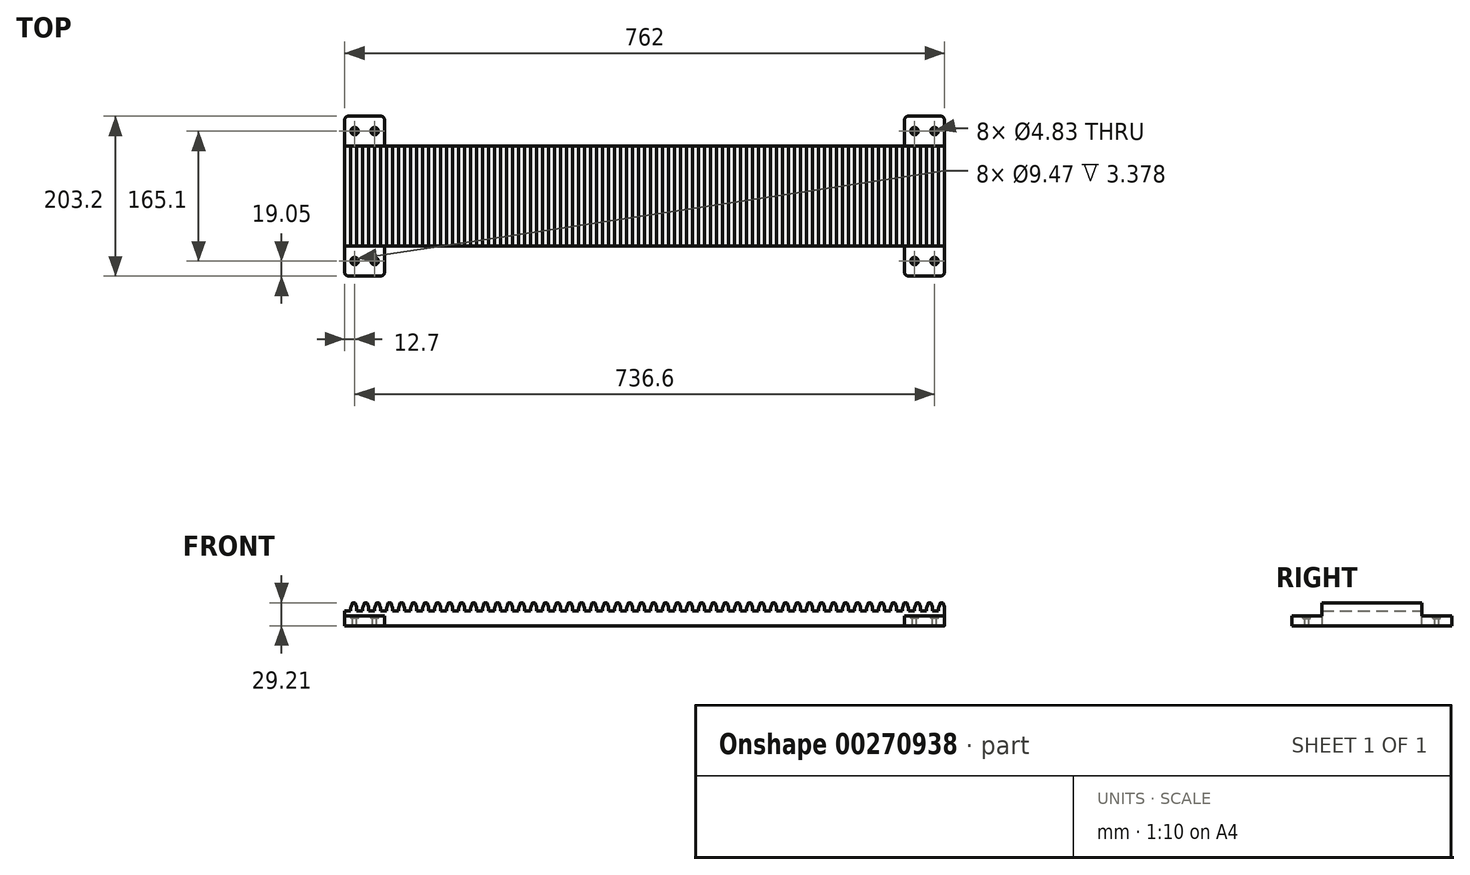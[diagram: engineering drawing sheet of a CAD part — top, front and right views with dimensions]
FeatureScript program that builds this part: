
annotation { "Feature Type Name" : "Feature", "Feature Type Description" : "" }
export const myFeature = defineFeature(function(context is Context, id is Id, definition is map)
    precondition{}
    {
        {
            var Q0;
            Q0=qCreatedBy(makeId("Front.planeOp"),FACE);
            var sketch = newSketch(context, id + "F0", { "sketchPlane" : qUnion([Q0])});
            skLineSegment(sketch, "E0", {"start": v(0, 0) * mm, "end": v(7.62, 0) * mm});
            skLineSegment(sketch, "E1", {"start": v(7.62, 0) * mm, "end": v(7.62, 2.76) * mm});
            skLineSegment(sketch, "E2", {"start": v(7.62, 0) * mm, "end": v(15.24, 0) * mm});
            skLineSegment(sketch, "E3", {"start": v(15.24, 0) * mm, "end": v(15.24, 2.76) * mm});
            skLineSegment(sketch, "E4", {"start": v(9.77, 9.65) * mm, "end": v(8.02, 4.99) * mm});
            skLineSegment(sketch, "E5", {"start": v(13.1, 9.65) * mm, "end": v(14.84, 4.99) * mm});
            skLineSegment(sketch, "E6", {"start": v(10.5, 10.16) * mm, "end": v(12.36, 10.16) * mm});
            skPoint(sketch, "E7.visualSharp", {"position": v(9.96, 10.16) * mm});
            skArc(sketch, "E7.filletArc", {"start": v(10.5, 10.16) * mm, "mid": v(10.05, 10.02) * mm, "end": v(9.77, 9.65) * mm});
            skPoint(sketch, "E8.visualSharp", {"position": v(12.9, 10.16) * mm});
            skArc(sketch, "E8.filletArc", {"start": v(13.1, 9.65) * mm, "mid": v(12.8, 10.02) * mm, "end": v(12.36, 10.16) * mm});
            skPoint(sketch, "E9.visualSharp", {"position": v(7.62, 3.91) * mm});
            skArc(sketch, "E9.filletArc", {"start": v(8.02, 4.99) * mm, "mid": v(7.72, 3.9) * mm, "end": v(7.62, 2.76) * mm});
            skPoint(sketch, "E10.visualSharp", {"position": v(15.24, 3.91) * mm});
            skArc(sketch, "E10.filletArc", {"start": v(15.24, 2.76) * mm, "mid": v(15.14, 3.9) * mm, "end": v(14.84, 4.99) * mm});
            skLineSegment(sketch, "E11", {"start": v(0, 0) * mm, "end": v(0, -19.05) * mm});
            skLineSegment(sketch, "E12", {"start": v(0, -19.05) * mm, "end": v(762, -19.05) * mm});
            skLineSegment(sketch, "E13", {"start": v(762, 0) * mm, "end": v(15.24, 0) * mm});
            skLineSegment(sketch, "E14", {"start": v(15.24, 0) * mm, "end": v(22.86, 0) * mm});
            skLineSegment(sketch, "E15.1.0.0", {"start": v(22.86, 0) * mm, "end": v(22.86, 2.76) * mm});
            skArc(sketch, "E15.1.0.1", {"start": v(23.26, 4.99) * mm, "mid": v(22.96, 3.9) * mm, "end": v(22.86, 2.76) * mm});
            skLineSegment(sketch, "E15.1.0.2", {"start": v(25, 9.65) * mm, "end": v(23.26, 4.99) * mm});
            skArc(sketch, "E15.1.0.3", {"start": v(25.74, 10.16) * mm, "mid": v(25.3, 10.02) * mm, "end": v(25, 9.65) * mm});
            skLineSegment(sketch, "E15.1.0.4", {"start": v(25.74, 10.16) * mm, "end": v(27.6, 10.16) * mm});
            skArc(sketch, "E15.1.0.5", {"start": v(28.33, 9.65) * mm, "mid": v(28.05, 10.02) * mm, "end": v(27.6, 10.16) * mm});
            skLineSegment(sketch, "E15.1.0.6", {"start": v(28.33, 9.65) * mm, "end": v(30.08, 4.99) * mm});
            skArc(sketch, "E15.1.0.7", {"start": v(30.48, 2.76) * mm, "mid": v(30.38, 3.9) * mm, "end": v(30.08, 4.99) * mm});
            skLineSegment(sketch, "E15.1.0.8", {"start": v(30.48, 0) * mm, "end": v(30.48, 2.76) * mm});
            skLineSegment(sketch, "E15.2.0.0", {"start": v(38.1, 0) * mm, "end": v(38.1, 2.76) * mm});
            skArc(sketch, "E15.2.0.1", {"start": v(38.5, 4.99) * mm, "mid": v(38.2, 3.9) * mm, "end": v(38.1, 2.76) * mm});
            skLineSegment(sketch, "E15.2.0.2", {"start": v(40.25, 9.65) * mm, "end": v(38.5, 4.99) * mm});
            skArc(sketch, "E15.2.0.3", {"start": v(40.98, 10.16) * mm, "mid": v(40.53, 10.02) * mm, "end": v(40.25, 9.65) * mm});
            skLineSegment(sketch, "E15.2.0.4", {"start": v(40.98, 10.16) * mm, "end": v(42.84, 10.16) * mm});
            skArc(sketch, "E15.2.0.5", {"start": v(43.57, 9.65) * mm, "mid": v(43.29, 10.02) * mm, "end": v(42.84, 10.16) * mm});
            skLineSegment(sketch, "E15.2.0.6", {"start": v(43.57, 9.65) * mm, "end": v(45.32, 4.99) * mm});
            skArc(sketch, "E15.2.0.7", {"start": v(45.72, 2.76) * mm, "mid": v(45.62, 3.9) * mm, "end": v(45.32, 4.99) * mm});
            skLineSegment(sketch, "E15.2.0.8", {"start": v(45.72, 0) * mm, "end": v(45.72, 2.76) * mm});
            skLineSegment(sketch, "E15.3.0.0", {"start": v(53.34, 0) * mm, "end": v(53.34, 2.76) * mm});
            skArc(sketch, "E15.3.0.1", {"start": v(53.74, 4.99) * mm, "mid": v(53.44, 3.9) * mm, "end": v(53.34, 2.76) * mm});
            skLineSegment(sketch, "E15.3.0.2", {"start": v(55.49, 9.65) * mm, "end": v(53.74, 4.99) * mm});
            skArc(sketch, "E15.3.0.3", {"start": v(56.22, 10.16) * mm, "mid": v(55.77, 10.02) * mm, "end": v(55.49, 9.65) * mm});
            skLineSegment(sketch, "E15.3.0.4", {"start": v(56.22, 10.16) * mm, "end": v(58.08, 10.16) * mm});
            skArc(sketch, "E15.3.0.5", {"start": v(58.81, 9.65) * mm, "mid": v(58.53, 10.02) * mm, "end": v(58.08, 10.16) * mm});
            skLineSegment(sketch, "E15.3.0.6", {"start": v(58.81, 9.65) * mm, "end": v(60.56, 4.99) * mm});
            skArc(sketch, "E15.3.0.7", {"start": v(60.96, 2.76) * mm, "mid": v(60.86, 3.9) * mm, "end": v(60.56, 4.99) * mm});
            skLineSegment(sketch, "E15.3.0.8", {"start": v(60.96, 0) * mm, "end": v(60.96, 2.76) * mm});
            skLineSegment(sketch, "E15.4.0.0", {"start": v(68.58, 0) * mm, "end": v(68.58, 2.76) * mm});
            skArc(sketch, "E15.4.0.1", {"start": v(68.98, 4.99) * mm, "mid": v(68.68, 3.9) * mm, "end": v(68.58, 2.76) * mm});
            skLineSegment(sketch, "E15.4.0.2", {"start": v(70.73, 9.65) * mm, "end": v(68.98, 4.99) * mm});
            skArc(sketch, "E15.4.0.3", {"start": v(71.46, 10.16) * mm, "mid": v(71.01, 10.02) * mm, "end": v(70.73, 9.65) * mm});
            skLineSegment(sketch, "E15.4.0.4", {"start": v(71.46, 10.16) * mm, "end": v(73.32, 10.16) * mm});
            skArc(sketch, "E15.4.0.5", {"start": v(74.05, 9.65) * mm, "mid": v(73.77, 10.02) * mm, "end": v(73.32, 10.16) * mm});
            skLineSegment(sketch, "E15.4.0.6", {"start": v(74.05, 9.65) * mm, "end": v(75.8, 4.99) * mm});
            skArc(sketch, "E15.4.0.7", {"start": v(76.2, 2.76) * mm, "mid": v(76.1, 3.9) * mm, "end": v(75.8, 4.99) * mm});
            skLineSegment(sketch, "E15.4.0.8", {"start": v(76.2, 0) * mm, "end": v(76.2, 2.76) * mm});
            skLineSegment(sketch, "E15.5.0.0", {"start": v(83.82, 0) * mm, "end": v(83.82, 2.76) * mm});
            skArc(sketch, "E15.5.0.1", {"start": v(84.22, 4.99) * mm, "mid": v(83.92, 3.9) * mm, "end": v(83.82, 2.76) * mm});
            skLineSegment(sketch, "E15.5.0.2", {"start": v(85.97, 9.65) * mm, "end": v(84.22, 4.99) * mm});
            skArc(sketch, "E15.5.0.3", {"start": v(86.7, 10.16) * mm, "mid": v(86.25, 10.02) * mm, "end": v(85.97, 9.65) * mm});
            skLineSegment(sketch, "E15.5.0.4", {"start": v(86.7, 10.16) * mm, "end": v(88.56, 10.16) * mm});
            skArc(sketch, "E15.5.0.5", {"start": v(89.3, 9.65) * mm, "mid": v(89, 10.02) * mm, "end": v(88.56, 10.16) * mm});
            skLineSegment(sketch, "E15.5.0.6", {"start": v(89.3, 9.65) * mm, "end": v(91.04, 4.99) * mm});
            skArc(sketch, "E15.5.0.7", {"start": v(91.44, 2.76) * mm, "mid": v(91.34, 3.9) * mm, "end": v(91.04, 4.99) * mm});
            skLineSegment(sketch, "E15.5.0.8", {"start": v(91.44, 0) * mm, "end": v(91.44, 2.76) * mm});
            skLineSegment(sketch, "E15.6.0.0", {"start": v(99.06, 0) * mm, "end": v(99.06, 2.76) * mm});
            skArc(sketch, "E15.6.0.1", {"start": v(99.46, 4.99) * mm, "mid": v(99.16, 3.9) * mm, "end": v(99.06, 2.76) * mm});
            skLineSegment(sketch, "E15.6.0.2", {"start": v(101.2, 9.65) * mm, "end": v(99.46, 4.99) * mm});
            skArc(sketch, "E15.6.0.3", {"start": v(101.94, 10.16) * mm, "mid": v(101.5, 10.02) * mm, "end": v(101.2, 9.65) * mm});
            skLineSegment(sketch, "E15.6.0.4", {"start": v(101.94, 10.16) * mm, "end": v(103.8, 10.16) * mm});
            skArc(sketch, "E15.6.0.5", {"start": v(104.53, 9.65) * mm, "mid": v(104.25, 10.02) * mm, "end": v(103.8, 10.16) * mm});
            skLineSegment(sketch, "E15.6.0.6", {"start": v(104.53, 9.65) * mm, "end": v(106.28, 4.99) * mm});
            skArc(sketch, "E15.6.0.7", {"start": v(106.68, 2.76) * mm, "mid": v(106.58, 3.9) * mm, "end": v(106.28, 4.99) * mm});
            skLineSegment(sketch, "E15.6.0.8", {"start": v(106.68, 0) * mm, "end": v(106.68, 2.76) * mm});
            skLineSegment(sketch, "E15.7.0.0", {"start": v(114.3, 0) * mm, "end": v(114.3, 2.76) * mm});
            skArc(sketch, "E15.7.0.1", {"start": v(114.7, 4.99) * mm, "mid": v(114.4, 3.9) * mm, "end": v(114.3, 2.76) * mm});
            skLineSegment(sketch, "E15.7.0.2", {"start": v(116.45, 9.65) * mm, "end": v(114.7, 4.99) * mm});
            skArc(sketch, "E15.7.0.3", {"start": v(117.18, 10.16) * mm, "mid": v(116.73, 10.02) * mm, "end": v(116.45, 9.65) * mm});
            skLineSegment(sketch, "E15.7.0.4", {"start": v(117.18, 10.16) * mm, "end": v(119.04, 10.16) * mm});
            skArc(sketch, "E15.7.0.5", {"start": v(119.77, 9.65) * mm, "mid": v(119.49, 10.02) * mm, "end": v(119.04, 10.16) * mm});
            skLineSegment(sketch, "E15.7.0.6", {"start": v(119.77, 9.65) * mm, "end": v(121.52, 4.99) * mm});
            skArc(sketch, "E15.7.0.7", {"start": v(121.92, 2.76) * mm, "mid": v(121.82, 3.9) * mm, "end": v(121.52, 4.99) * mm});
            skLineSegment(sketch, "E15.7.0.8", {"start": v(121.92, 0) * mm, "end": v(121.92, 2.76) * mm});
            skLineSegment(sketch, "E15.8.0.0", {"start": v(129.54, 0) * mm, "end": v(129.54, 2.76) * mm});
            skArc(sketch, "E15.8.0.1", {"start": v(129.94, 4.99) * mm, "mid": v(129.64, 3.9) * mm, "end": v(129.54, 2.76) * mm});
            skLineSegment(sketch, "E15.8.0.2", {"start": v(131.69, 9.65) * mm, "end": v(129.94, 4.99) * mm});
            skArc(sketch, "E15.8.0.3", {"start": v(132.42, 10.16) * mm, "mid": v(131.97, 10.02) * mm, "end": v(131.69, 9.65) * mm});
            skLineSegment(sketch, "E15.8.0.4", {"start": v(132.42, 10.16) * mm, "end": v(134.28, 10.16) * mm});
            skArc(sketch, "E15.8.0.5", {"start": v(135.01, 9.65) * mm, "mid": v(134.73, 10.02) * mm, "end": v(134.28, 10.16) * mm});
            skLineSegment(sketch, "E15.8.0.6", {"start": v(135.01, 9.65) * mm, "end": v(136.76, 4.99) * mm});
            skArc(sketch, "E15.8.0.7", {"start": v(137.16, 2.76) * mm, "mid": v(137.06, 3.9) * mm, "end": v(136.76, 4.99) * mm});
            skLineSegment(sketch, "E15.8.0.8", {"start": v(137.16, 0) * mm, "end": v(137.16, 2.76) * mm});
            skLineSegment(sketch, "E15.9.0.0", {"start": v(144.78, 0) * mm, "end": v(144.78, 2.76) * mm});
            skArc(sketch, "E15.9.0.1", {"start": v(145.18, 4.99) * mm, "mid": v(144.88, 3.9) * mm, "end": v(144.78, 2.76) * mm});
            skLineSegment(sketch, "E15.9.0.2", {"start": v(146.93, 9.65) * mm, "end": v(145.18, 4.99) * mm});
            skArc(sketch, "E15.9.0.3", {"start": v(147.66, 10.16) * mm, "mid": v(147.21, 10.02) * mm, "end": v(146.93, 9.65) * mm});
            skLineSegment(sketch, "E15.9.0.4", {"start": v(147.66, 10.16) * mm, "end": v(149.52, 10.16) * mm});
            skArc(sketch, "E15.9.0.5", {"start": v(150.25, 9.65) * mm, "mid": v(149.97, 10.02) * mm, "end": v(149.52, 10.16) * mm});
            skLineSegment(sketch, "E15.9.0.6", {"start": v(150.25, 9.65) * mm, "end": v(152, 4.99) * mm});
            skArc(sketch, "E15.9.0.7", {"start": v(152.4, 2.76) * mm, "mid": v(152.3, 3.9) * mm, "end": v(152, 4.99) * mm});
            skLineSegment(sketch, "E15.9.0.8", {"start": v(152.4, 0) * mm, "end": v(152.4, 2.76) * mm});
            skLineSegment(sketch, "E15.10.0.0", {"start": v(160.02, 0) * mm, "end": v(160.02, 2.76) * mm});
            skArc(sketch, "E15.10.0.1", {"start": v(160.42, 4.99) * mm, "mid": v(160.12, 3.9) * mm, "end": v(160.02, 2.76) * mm});
            skLineSegment(sketch, "E15.10.0.2", {"start": v(162.17, 9.65) * mm, "end": v(160.42, 4.99) * mm});
            skArc(sketch, "E15.10.0.3", {"start": v(162.9, 10.16) * mm, "mid": v(162.45, 10.02) * mm, "end": v(162.17, 9.65) * mm});
            skLineSegment(sketch, "E15.10.0.4", {"start": v(162.9, 10.16) * mm, "end": v(164.76, 10.16) * mm});
            skArc(sketch, "E15.10.0.5", {"start": v(165.5, 9.65) * mm, "mid": v(165.2, 10.02) * mm, "end": v(164.76, 10.16) * mm});
            skLineSegment(sketch, "E15.10.0.6", {"start": v(165.5, 9.65) * mm, "end": v(167.24, 4.99) * mm});
            skArc(sketch, "E15.10.0.7", {"start": v(167.64, 2.76) * mm, "mid": v(167.54, 3.9) * mm, "end": v(167.24, 4.99) * mm});
            skLineSegment(sketch, "E15.10.0.8", {"start": v(167.64, 0) * mm, "end": v(167.64, 2.76) * mm});
            skLineSegment(sketch, "E15.11.0.0", {"start": v(175.26, 0) * mm, "end": v(175.26, 2.76) * mm});
            skArc(sketch, "E15.11.0.1", {"start": v(175.66, 4.99) * mm, "mid": v(175.36, 3.9) * mm, "end": v(175.26, 2.76) * mm});
            skLineSegment(sketch, "E15.11.0.2", {"start": v(177.4, 9.65) * mm, "end": v(175.66, 4.99) * mm});
            skArc(sketch, "E15.11.0.3", {"start": v(178.14, 10.16) * mm, "mid": v(177.7, 10.02) * mm, "end": v(177.4, 9.65) * mm});
            skLineSegment(sketch, "E15.11.0.4", {"start": v(178.14, 10.16) * mm, "end": v(180, 10.16) * mm});
            skArc(sketch, "E15.11.0.5", {"start": v(180.73, 9.65) * mm, "mid": v(180.45, 10.02) * mm, "end": v(180, 10.16) * mm});
            skLineSegment(sketch, "E15.11.0.6", {"start": v(180.73, 9.65) * mm, "end": v(182.48, 4.99) * mm});
            skArc(sketch, "E15.11.0.7", {"start": v(182.88, 2.76) * mm, "mid": v(182.78, 3.9) * mm, "end": v(182.48, 4.99) * mm});
            skLineSegment(sketch, "E15.11.0.8", {"start": v(182.88, 0) * mm, "end": v(182.88, 2.76) * mm});
            skLineSegment(sketch, "E15.12.0.0", {"start": v(190.5, 0) * mm, "end": v(190.5, 2.76) * mm});
            skArc(sketch, "E15.12.0.1", {"start": v(190.9, 4.99) * mm, "mid": v(190.6, 3.9) * mm, "end": v(190.5, 2.76) * mm});
            skLineSegment(sketch, "E15.12.0.2", {"start": v(192.65, 9.65) * mm, "end": v(190.9, 4.99) * mm});
            skArc(sketch, "E15.12.0.3", {"start": v(193.38, 10.16) * mm, "mid": v(192.93, 10.02) * mm, "end": v(192.65, 9.65) * mm});
            skLineSegment(sketch, "E15.12.0.4", {"start": v(193.38, 10.16) * mm, "end": v(195.24, 10.16) * mm});
            skArc(sketch, "E15.12.0.5", {"start": v(195.97, 9.65) * mm, "mid": v(195.69, 10.02) * mm, "end": v(195.24, 10.16) * mm});
            skLineSegment(sketch, "E15.12.0.6", {"start": v(195.97, 9.65) * mm, "end": v(197.72, 4.99) * mm});
            skArc(sketch, "E15.12.0.7", {"start": v(198.12, 2.76) * mm, "mid": v(198.02, 3.9) * mm, "end": v(197.72, 4.99) * mm});
            skLineSegment(sketch, "E15.12.0.8", {"start": v(198.12, 0) * mm, "end": v(198.12, 2.76) * mm});
            skLineSegment(sketch, "E15.13.0.0", {"start": v(205.74, 0) * mm, "end": v(205.74, 2.76) * mm});
            skArc(sketch, "E15.13.0.1", {"start": v(206.14, 4.99) * mm, "mid": v(205.84, 3.9) * mm, "end": v(205.74, 2.76) * mm});
            skLineSegment(sketch, "E15.13.0.2", {"start": v(207.89, 9.65) * mm, "end": v(206.14, 4.99) * mm});
            skArc(sketch, "E15.13.0.3", {"start": v(208.62, 10.16) * mm, "mid": v(208.17, 10.02) * mm, "end": v(207.89, 9.65) * mm});
            skLineSegment(sketch, "E15.13.0.4", {"start": v(208.62, 10.16) * mm, "end": v(210.48, 10.16) * mm});
            skArc(sketch, "E15.13.0.5", {"start": v(211.21, 9.65) * mm, "mid": v(210.93, 10.02) * mm, "end": v(210.48, 10.16) * mm});
            skLineSegment(sketch, "E15.13.0.6", {"start": v(211.21, 9.65) * mm, "end": v(212.96, 4.99) * mm});
            skArc(sketch, "E15.13.0.7", {"start": v(213.36, 2.76) * mm, "mid": v(213.26, 3.9) * mm, "end": v(212.96, 4.99) * mm});
            skLineSegment(sketch, "E15.13.0.8", {"start": v(213.36, 0) * mm, "end": v(213.36, 2.76) * mm});
            skLineSegment(sketch, "E15.14.0.0", {"start": v(220.98, 0) * mm, "end": v(220.98, 2.76) * mm});
            skArc(sketch, "E15.14.0.1", {"start": v(221.38, 4.99) * mm, "mid": v(221.08, 3.9) * mm, "end": v(220.98, 2.76) * mm});
            skLineSegment(sketch, "E15.14.0.2", {"start": v(223.13, 9.65) * mm, "end": v(221.38, 4.99) * mm});
            skArc(sketch, "E15.14.0.3", {"start": v(223.86, 10.16) * mm, "mid": v(223.41, 10.02) * mm, "end": v(223.13, 9.65) * mm});
            skLineSegment(sketch, "E15.14.0.4", {"start": v(223.86, 10.16) * mm, "end": v(225.72, 10.16) * mm});
            skArc(sketch, "E15.14.0.5", {"start": v(226.45, 9.65) * mm, "mid": v(226.17, 10.02) * mm, "end": v(225.72, 10.16) * mm});
            skLineSegment(sketch, "E15.14.0.6", {"start": v(226.45, 9.65) * mm, "end": v(228.2, 4.99) * mm});
            skArc(sketch, "E15.14.0.7", {"start": v(228.6, 2.76) * mm, "mid": v(228.5, 3.9) * mm, "end": v(228.2, 4.99) * mm});
            skLineSegment(sketch, "E15.14.0.8", {"start": v(228.6, 0) * mm, "end": v(228.6, 2.76) * mm});
            skLineSegment(sketch, "E15.15.0.0", {"start": v(236.22, 0) * mm, "end": v(236.22, 2.76) * mm});
            skArc(sketch, "E15.15.0.1", {"start": v(236.62, 4.99) * mm, "mid": v(236.32, 3.9) * mm, "end": v(236.22, 2.76) * mm});
            skLineSegment(sketch, "E15.15.0.2", {"start": v(238.37, 9.65) * mm, "end": v(236.62, 4.99) * mm});
            skArc(sketch, "E15.15.0.3", {"start": v(239.1, 10.16) * mm, "mid": v(238.65, 10.02) * mm, "end": v(238.37, 9.65) * mm});
            skLineSegment(sketch, "E15.15.0.4", {"start": v(239.1, 10.16) * mm, "end": v(240.96, 10.16) * mm});
            skArc(sketch, "E15.15.0.5", {"start": v(241.7, 9.65) * mm, "mid": v(241.4, 10.02) * mm, "end": v(240.96, 10.16) * mm});
            skLineSegment(sketch, "E15.15.0.6", {"start": v(241.7, 9.65) * mm, "end": v(243.44, 4.99) * mm});
            skArc(sketch, "E15.15.0.7", {"start": v(243.84, 2.76) * mm, "mid": v(243.74, 3.9) * mm, "end": v(243.44, 4.99) * mm});
            skLineSegment(sketch, "E15.15.0.8", {"start": v(243.84, 0) * mm, "end": v(243.84, 2.76) * mm});
            skLineSegment(sketch, "E15.16.0.0", {"start": v(251.46, 0) * mm, "end": v(251.46, 2.76) * mm});
            skArc(sketch, "E15.16.0.1", {"start": v(251.86, 4.99) * mm, "mid": v(251.56, 3.9) * mm, "end": v(251.46, 2.76) * mm});
            skLineSegment(sketch, "E15.16.0.2", {"start": v(253.6, 9.65) * mm, "end": v(251.86, 4.99) * mm});
            skArc(sketch, "E15.16.0.3", {"start": v(254.34, 10.16) * mm, "mid": v(253.9, 10.02) * mm, "end": v(253.6, 9.65) * mm});
            skLineSegment(sketch, "E15.16.0.4", {"start": v(254.34, 10.16) * mm, "end": v(256.2, 10.16) * mm});
            skArc(sketch, "E15.16.0.5", {"start": v(256.93, 9.65) * mm, "mid": v(256.65, 10.02) * mm, "end": v(256.2, 10.16) * mm});
            skLineSegment(sketch, "E15.16.0.6", {"start": v(256.93, 9.65) * mm, "end": v(258.68, 4.99) * mm});
            skArc(sketch, "E15.16.0.7", {"start": v(259.08, 2.76) * mm, "mid": v(258.98, 3.9) * mm, "end": v(258.68, 4.99) * mm});
            skLineSegment(sketch, "E15.16.0.8", {"start": v(259.08, 0) * mm, "end": v(259.08, 2.76) * mm});
            skLineSegment(sketch, "E15.17.0.0", {"start": v(266.7, 0) * mm, "end": v(266.7, 2.76) * mm});
            skArc(sketch, "E15.17.0.1", {"start": v(267.1, 4.99) * mm, "mid": v(266.8, 3.9) * mm, "end": v(266.7, 2.76) * mm});
            skLineSegment(sketch, "E15.17.0.2", {"start": v(268.85, 9.65) * mm, "end": v(267.1, 4.99) * mm});
            skArc(sketch, "E15.17.0.3", {"start": v(269.58, 10.16) * mm, "mid": v(269.13, 10.02) * mm, "end": v(268.85, 9.65) * mm});
            skLineSegment(sketch, "E15.17.0.4", {"start": v(269.58, 10.16) * mm, "end": v(271.44, 10.16) * mm});
            skArc(sketch, "E15.17.0.5", {"start": v(272.17, 9.65) * mm, "mid": v(271.89, 10.02) * mm, "end": v(271.44, 10.16) * mm});
            skLineSegment(sketch, "E15.17.0.6", {"start": v(272.17, 9.65) * mm, "end": v(273.92, 4.99) * mm});
            skArc(sketch, "E15.17.0.7", {"start": v(274.32, 2.76) * mm, "mid": v(274.22, 3.9) * mm, "end": v(273.92, 4.99) * mm});
            skLineSegment(sketch, "E15.17.0.8", {"start": v(274.32, 0) * mm, "end": v(274.32, 2.76) * mm});
            skLineSegment(sketch, "E15.18.0.0", {"start": v(281.94, 0) * mm, "end": v(281.94, 2.76) * mm});
            skArc(sketch, "E15.18.0.1", {"start": v(282.34, 4.99) * mm, "mid": v(282.04, 3.9) * mm, "end": v(281.94, 2.76) * mm});
            skLineSegment(sketch, "E15.18.0.2", {"start": v(284.09, 9.65) * mm, "end": v(282.34, 4.99) * mm});
            skArc(sketch, "E15.18.0.3", {"start": v(284.82, 10.16) * mm, "mid": v(284.37, 10.02) * mm, "end": v(284.09, 9.65) * mm});
            skLineSegment(sketch, "E15.18.0.4", {"start": v(284.82, 10.16) * mm, "end": v(286.68, 10.16) * mm});
            skArc(sketch, "E15.18.0.5", {"start": v(287.41, 9.65) * mm, "mid": v(287.13, 10.02) * mm, "end": v(286.68, 10.16) * mm});
            skLineSegment(sketch, "E15.18.0.6", {"start": v(287.41, 9.65) * mm, "end": v(289.16, 4.99) * mm});
            skArc(sketch, "E15.18.0.7", {"start": v(289.56, 2.76) * mm, "mid": v(289.46, 3.9) * mm, "end": v(289.16, 4.99) * mm});
            skLineSegment(sketch, "E15.18.0.8", {"start": v(289.56, 0) * mm, "end": v(289.56, 2.76) * mm});
            skLineSegment(sketch, "E15.19.0.0", {"start": v(297.18, 0) * mm, "end": v(297.18, 2.76) * mm});
            skArc(sketch, "E15.19.0.1", {"start": v(297.58, 4.99) * mm, "mid": v(297.28, 3.9) * mm, "end": v(297.18, 2.76) * mm});
            skLineSegment(sketch, "E15.19.0.2", {"start": v(299.33, 9.65) * mm, "end": v(297.58, 4.99) * mm});
            skArc(sketch, "E15.19.0.3", {"start": v(300.06, 10.16) * mm, "mid": v(299.61, 10.02) * mm, "end": v(299.33, 9.65) * mm});
            skLineSegment(sketch, "E15.19.0.4", {"start": v(300.06, 10.16) * mm, "end": v(301.92, 10.16) * mm});
            skArc(sketch, "E15.19.0.5", {"start": v(302.65, 9.65) * mm, "mid": v(302.37, 10.02) * mm, "end": v(301.92, 10.16) * mm});
            skLineSegment(sketch, "E15.19.0.6", {"start": v(302.65, 9.65) * mm, "end": v(304.4, 4.99) * mm});
            skArc(sketch, "E15.19.0.7", {"start": v(304.8, 2.76) * mm, "mid": v(304.7, 3.9) * mm, "end": v(304.4, 4.99) * mm});
            skLineSegment(sketch, "E15.19.0.8", {"start": v(304.8, 0) * mm, "end": v(304.8, 2.76) * mm});
            skLineSegment(sketch, "E15.20.0.0", {"start": v(312.42, 0) * mm, "end": v(312.42, 2.76) * mm});
            skArc(sketch, "E15.20.0.1", {"start": v(312.82, 4.99) * mm, "mid": v(312.52, 3.9) * mm, "end": v(312.42, 2.76) * mm});
            skLineSegment(sketch, "E15.20.0.2", {"start": v(314.57, 9.65) * mm, "end": v(312.82, 4.99) * mm});
            skArc(sketch, "E15.20.0.3", {"start": v(315.3, 10.16) * mm, "mid": v(314.85, 10.02) * mm, "end": v(314.57, 9.65) * mm});
            skLineSegment(sketch, "E15.20.0.4", {"start": v(315.3, 10.16) * mm, "end": v(317.16, 10.16) * mm});
            skArc(sketch, "E15.20.0.5", {"start": v(317.9, 9.65) * mm, "mid": v(317.6, 10.02) * mm, "end": v(317.16, 10.16) * mm});
            skLineSegment(sketch, "E15.20.0.6", {"start": v(317.9, 9.65) * mm, "end": v(319.64, 4.99) * mm});
            skArc(sketch, "E15.20.0.7", {"start": v(320.04, 2.76) * mm, "mid": v(319.94, 3.9) * mm, "end": v(319.64, 4.99) * mm});
            skLineSegment(sketch, "E15.20.0.8", {"start": v(320.04, 0) * mm, "end": v(320.04, 2.76) * mm});
            skLineSegment(sketch, "E15.21.0.0", {"start": v(327.66, 0) * mm, "end": v(327.66, 2.76) * mm});
            skArc(sketch, "E15.21.0.1", {"start": v(328.06, 4.99) * mm, "mid": v(327.76, 3.9) * mm, "end": v(327.66, 2.76) * mm});
            skLineSegment(sketch, "E15.21.0.2", {"start": v(329.8, 9.65) * mm, "end": v(328.06, 4.99) * mm});
            skArc(sketch, "E15.21.0.3", {"start": v(330.54, 10.16) * mm, "mid": v(330.1, 10.02) * mm, "end": v(329.8, 9.65) * mm});
            skLineSegment(sketch, "E15.21.0.4", {"start": v(330.54, 10.16) * mm, "end": v(332.4, 10.16) * mm});
            skArc(sketch, "E15.21.0.5", {"start": v(333.13, 9.65) * mm, "mid": v(332.85, 10.02) * mm, "end": v(332.4, 10.16) * mm});
            skLineSegment(sketch, "E15.21.0.6", {"start": v(333.13, 9.65) * mm, "end": v(334.88, 4.99) * mm});
            skArc(sketch, "E15.21.0.7", {"start": v(335.28, 2.76) * mm, "mid": v(335.18, 3.9) * mm, "end": v(334.88, 4.99) * mm});
            skLineSegment(sketch, "E15.21.0.8", {"start": v(335.28, 0) * mm, "end": v(335.28, 2.76) * mm});
            skLineSegment(sketch, "E15.22.0.0", {"start": v(342.9, 0) * mm, "end": v(342.9, 2.76) * mm});
            skArc(sketch, "E15.22.0.1", {"start": v(343.3, 4.99) * mm, "mid": v(343, 3.9) * mm, "end": v(342.9, 2.76) * mm});
            skLineSegment(sketch, "E15.22.0.2", {"start": v(345.05, 9.65) * mm, "end": v(343.3, 4.99) * mm});
            skArc(sketch, "E15.22.0.3", {"start": v(345.78, 10.16) * mm, "mid": v(345.33, 10.02) * mm, "end": v(345.05, 9.65) * mm});
            skLineSegment(sketch, "E15.22.0.4", {"start": v(345.78, 10.16) * mm, "end": v(347.64, 10.16) * mm});
            skArc(sketch, "E15.22.0.5", {"start": v(348.37, 9.65) * mm, "mid": v(348.09, 10.02) * mm, "end": v(347.64, 10.16) * mm});
            skLineSegment(sketch, "E15.22.0.6", {"start": v(348.37, 9.65) * mm, "end": v(350.12, 4.99) * mm});
            skArc(sketch, "E15.22.0.7", {"start": v(350.52, 2.76) * mm, "mid": v(350.42, 3.9) * mm, "end": v(350.12, 4.99) * mm});
            skLineSegment(sketch, "E15.22.0.8", {"start": v(350.52, 0) * mm, "end": v(350.52, 2.76) * mm});
            skLineSegment(sketch, "E15.23.0.0", {"start": v(358.14, 0) * mm, "end": v(358.14, 2.76) * mm});
            skArc(sketch, "E15.23.0.1", {"start": v(358.54, 4.99) * mm, "mid": v(358.24, 3.9) * mm, "end": v(358.14, 2.76) * mm});
            skLineSegment(sketch, "E15.23.0.2", {"start": v(360.29, 9.65) * mm, "end": v(358.54, 4.99) * mm});
            skArc(sketch, "E15.23.0.3", {"start": v(361.02, 10.16) * mm, "mid": v(360.57, 10.02) * mm, "end": v(360.29, 9.65) * mm});
            skLineSegment(sketch, "E15.23.0.4", {"start": v(361.02, 10.16) * mm, "end": v(362.88, 10.16) * mm});
            skArc(sketch, "E15.23.0.5", {"start": v(363.61, 9.65) * mm, "mid": v(363.33, 10.02) * mm, "end": v(362.88, 10.16) * mm});
            skLineSegment(sketch, "E15.23.0.6", {"start": v(363.61, 9.65) * mm, "end": v(365.36, 4.99) * mm});
            skArc(sketch, "E15.23.0.7", {"start": v(365.76, 2.76) * mm, "mid": v(365.66, 3.9) * mm, "end": v(365.36, 4.99) * mm});
            skLineSegment(sketch, "E15.23.0.8", {"start": v(365.76, 0) * mm, "end": v(365.76, 2.76) * mm});
            skLineSegment(sketch, "E15.24.0.0", {"start": v(373.38, 0) * mm, "end": v(373.38, 2.76) * mm});
            skArc(sketch, "E15.24.0.1", {"start": v(373.78, 4.99) * mm, "mid": v(373.48, 3.9) * mm, "end": v(373.38, 2.76) * mm});
            skLineSegment(sketch, "E15.24.0.2", {"start": v(375.53, 9.65) * mm, "end": v(373.78, 4.99) * mm});
            skArc(sketch, "E15.24.0.3", {"start": v(376.26, 10.16) * mm, "mid": v(375.81, 10.02) * mm, "end": v(375.53, 9.65) * mm});
            skLineSegment(sketch, "E15.24.0.4", {"start": v(376.26, 10.16) * mm, "end": v(378.12, 10.16) * mm});
            skArc(sketch, "E15.24.0.5", {"start": v(378.85, 9.65) * mm, "mid": v(378.57, 10.02) * mm, "end": v(378.12, 10.16) * mm});
            skLineSegment(sketch, "E15.24.0.6", {"start": v(378.85, 9.65) * mm, "end": v(380.6, 4.99) * mm});
            skArc(sketch, "E15.24.0.7", {"start": v(381, 2.76) * mm, "mid": v(380.9, 3.9) * mm, "end": v(380.6, 4.99) * mm});
            skLineSegment(sketch, "E15.24.0.8", {"start": v(381, 0) * mm, "end": v(381, 2.76) * mm});
            skLineSegment(sketch, "E15.25.0.0", {"start": v(388.62, 0) * mm, "end": v(388.62, 2.76) * mm});
            skArc(sketch, "E15.25.0.1", {"start": v(389.02, 4.99) * mm, "mid": v(388.72, 3.9) * mm, "end": v(388.62, 2.76) * mm});
            skLineSegment(sketch, "E15.25.0.2", {"start": v(390.77, 9.65) * mm, "end": v(389.02, 4.99) * mm});
            skArc(sketch, "E15.25.0.3", {"start": v(391.5, 10.16) * mm, "mid": v(391.05, 10.02) * mm, "end": v(390.77, 9.65) * mm});
            skLineSegment(sketch, "E15.25.0.4", {"start": v(391.5, 10.16) * mm, "end": v(393.36, 10.16) * mm});
            skArc(sketch, "E15.25.0.5", {"start": v(394.1, 9.65) * mm, "mid": v(393.8, 10.02) * mm, "end": v(393.36, 10.16) * mm});
            skLineSegment(sketch, "E15.25.0.6", {"start": v(394.1, 9.65) * mm, "end": v(395.84, 4.99) * mm});
            skArc(sketch, "E15.25.0.7", {"start": v(396.24, 2.76) * mm, "mid": v(396.14, 3.9) * mm, "end": v(395.84, 4.99) * mm});
            skLineSegment(sketch, "E15.25.0.8", {"start": v(396.24, 0) * mm, "end": v(396.24, 2.76) * mm});
            skLineSegment(sketch, "E15.26.0.0", {"start": v(403.86, 0) * mm, "end": v(403.86, 2.76) * mm});
            skArc(sketch, "E15.26.0.1", {"start": v(404.26, 4.99) * mm, "mid": v(403.96, 3.9) * mm, "end": v(403.86, 2.76) * mm});
            skLineSegment(sketch, "E15.26.0.2", {"start": v(406, 9.65) * mm, "end": v(404.26, 4.99) * mm});
            skArc(sketch, "E15.26.0.3", {"start": v(406.74, 10.16) * mm, "mid": v(406.3, 10.02) * mm, "end": v(406, 9.65) * mm});
            skLineSegment(sketch, "E15.26.0.4", {"start": v(406.74, 10.16) * mm, "end": v(408.6, 10.16) * mm});
            skArc(sketch, "E15.26.0.5", {"start": v(409.33, 9.65) * mm, "mid": v(409.05, 10.02) * mm, "end": v(408.6, 10.16) * mm});
            skLineSegment(sketch, "E15.26.0.6", {"start": v(409.33, 9.65) * mm, "end": v(411.08, 4.99) * mm});
            skArc(sketch, "E15.26.0.7", {"start": v(411.48, 2.76) * mm, "mid": v(411.38, 3.9) * mm, "end": v(411.08, 4.99) * mm});
            skLineSegment(sketch, "E15.26.0.8", {"start": v(411.48, 0) * mm, "end": v(411.48, 2.76) * mm});
            skLineSegment(sketch, "E15.27.0.0", {"start": v(419.1, 0) * mm, "end": v(419.1, 2.76) * mm});
            skArc(sketch, "E15.27.0.1", {"start": v(419.5, 4.99) * mm, "mid": v(419.2, 3.9) * mm, "end": v(419.1, 2.76) * mm});
            skLineSegment(sketch, "E15.27.0.2", {"start": v(421.25, 9.65) * mm, "end": v(419.5, 4.99) * mm});
            skArc(sketch, "E15.27.0.3", {"start": v(421.98, 10.16) * mm, "mid": v(421.53, 10.02) * mm, "end": v(421.25, 9.65) * mm});
            skLineSegment(sketch, "E15.27.0.4", {"start": v(421.98, 10.16) * mm, "end": v(423.84, 10.16) * mm});
            skArc(sketch, "E15.27.0.5", {"start": v(424.57, 9.65) * mm, "mid": v(424.29, 10.02) * mm, "end": v(423.84, 10.16) * mm});
            skLineSegment(sketch, "E15.27.0.6", {"start": v(424.57, 9.65) * mm, "end": v(426.32, 4.99) * mm});
            skArc(sketch, "E15.27.0.7", {"start": v(426.72, 2.76) * mm, "mid": v(426.62, 3.9) * mm, "end": v(426.32, 4.99) * mm});
            skLineSegment(sketch, "E15.27.0.8", {"start": v(426.72, 0) * mm, "end": v(426.72, 2.76) * mm});
            skLineSegment(sketch, "E15.28.0.0", {"start": v(434.34, 0) * mm, "end": v(434.34, 2.76) * mm});
            skArc(sketch, "E15.28.0.1", {"start": v(434.74, 4.99) * mm, "mid": v(434.44, 3.9) * mm, "end": v(434.34, 2.76) * mm});
            skLineSegment(sketch, "E15.28.0.2", {"start": v(436.49, 9.65) * mm, "end": v(434.74, 4.99) * mm});
            skArc(sketch, "E15.28.0.3", {"start": v(437.22, 10.16) * mm, "mid": v(436.77, 10.02) * mm, "end": v(436.49, 9.65) * mm});
            skLineSegment(sketch, "E15.28.0.4", {"start": v(437.22, 10.16) * mm, "end": v(439.08, 10.16) * mm});
            skArc(sketch, "E15.28.0.5", {"start": v(439.81, 9.65) * mm, "mid": v(439.53, 10.02) * mm, "end": v(439.08, 10.16) * mm});
            skLineSegment(sketch, "E15.28.0.6", {"start": v(439.81, 9.65) * mm, "end": v(441.56, 4.99) * mm});
            skArc(sketch, "E15.28.0.7", {"start": v(441.96, 2.76) * mm, "mid": v(441.86, 3.9) * mm, "end": v(441.56, 4.99) * mm});
            skLineSegment(sketch, "E15.28.0.8", {"start": v(441.96, 0) * mm, "end": v(441.96, 2.76) * mm});
            skLineSegment(sketch, "E15.29.0.0", {"start": v(449.58, 0) * mm, "end": v(449.58, 2.76) * mm});
            skArc(sketch, "E15.29.0.1", {"start": v(449.98, 4.99) * mm, "mid": v(449.68, 3.9) * mm, "end": v(449.58, 2.76) * mm});
            skLineSegment(sketch, "E15.29.0.2", {"start": v(451.73, 9.65) * mm, "end": v(449.98, 4.99) * mm});
            skArc(sketch, "E15.29.0.3", {"start": v(452.46, 10.16) * mm, "mid": v(452.01, 10.02) * mm, "end": v(451.73, 9.65) * mm});
            skLineSegment(sketch, "E15.29.0.4", {"start": v(452.46, 10.16) * mm, "end": v(454.32, 10.16) * mm});
            skArc(sketch, "E15.29.0.5", {"start": v(455.05, 9.65) * mm, "mid": v(454.77, 10.02) * mm, "end": v(454.32, 10.16) * mm});
            skLineSegment(sketch, "E15.29.0.6", {"start": v(455.05, 9.65) * mm, "end": v(456.8, 4.99) * mm});
            skArc(sketch, "E15.29.0.7", {"start": v(457.2, 2.76) * mm, "mid": v(457.1, 3.9) * mm, "end": v(456.8, 4.99) * mm});
            skLineSegment(sketch, "E15.29.0.8", {"start": v(457.2, 0) * mm, "end": v(457.2, 2.76) * mm});
            skLineSegment(sketch, "E15.30.0.0", {"start": v(464.82, 0) * mm, "end": v(464.82, 2.76) * mm});
            skArc(sketch, "E15.30.0.1", {"start": v(465.22, 4.99) * mm, "mid": v(464.92, 3.9) * mm, "end": v(464.82, 2.76) * mm});
            skLineSegment(sketch, "E15.30.0.2", {"start": v(466.97, 9.65) * mm, "end": v(465.22, 4.99) * mm});
            skArc(sketch, "E15.30.0.3", {"start": v(467.7, 10.16) * mm, "mid": v(467.25, 10.02) * mm, "end": v(466.97, 9.65) * mm});
            skLineSegment(sketch, "E15.30.0.4", {"start": v(467.7, 10.16) * mm, "end": v(469.56, 10.16) * mm});
            skArc(sketch, "E15.30.0.5", {"start": v(470.3, 9.65) * mm, "mid": v(470, 10.02) * mm, "end": v(469.56, 10.16) * mm});
            skLineSegment(sketch, "E15.30.0.6", {"start": v(470.3, 9.65) * mm, "end": v(472.04, 4.99) * mm});
            skArc(sketch, "E15.30.0.7", {"start": v(472.44, 2.76) * mm, "mid": v(472.34, 3.9) * mm, "end": v(472.04, 4.99) * mm});
            skLineSegment(sketch, "E15.30.0.8", {"start": v(472.44, 0) * mm, "end": v(472.44, 2.76) * mm});
            skLineSegment(sketch, "E15.31.0.0", {"start": v(480.06, 0) * mm, "end": v(480.06, 2.76) * mm});
            skArc(sketch, "E15.31.0.1", {"start": v(480.46, 4.99) * mm, "mid": v(480.16, 3.9) * mm, "end": v(480.06, 2.76) * mm});
            skLineSegment(sketch, "E15.31.0.2", {"start": v(482.2, 9.65) * mm, "end": v(480.46, 4.99) * mm});
            skArc(sketch, "E15.31.0.3", {"start": v(482.94, 10.16) * mm, "mid": v(482.5, 10.02) * mm, "end": v(482.2, 9.65) * mm});
            skLineSegment(sketch, "E15.31.0.4", {"start": v(482.94, 10.16) * mm, "end": v(484.8, 10.16) * mm});
            skArc(sketch, "E15.31.0.5", {"start": v(485.53, 9.65) * mm, "mid": v(485.25, 10.02) * mm, "end": v(484.8, 10.16) * mm});
            skLineSegment(sketch, "E15.31.0.6", {"start": v(485.53, 9.65) * mm, "end": v(487.28, 4.99) * mm});
            skArc(sketch, "E15.31.0.7", {"start": v(487.68, 2.76) * mm, "mid": v(487.58, 3.9) * mm, "end": v(487.28, 4.99) * mm});
            skLineSegment(sketch, "E15.31.0.8", {"start": v(487.68, 0) * mm, "end": v(487.68, 2.76) * mm});
            skLineSegment(sketch, "E15.32.0.0", {"start": v(495.3, 0) * mm, "end": v(495.3, 2.76) * mm});
            skArc(sketch, "E15.32.0.1", {"start": v(495.7, 4.99) * mm, "mid": v(495.4, 3.9) * mm, "end": v(495.3, 2.76) * mm});
            skLineSegment(sketch, "E15.32.0.2", {"start": v(497.45, 9.65) * mm, "end": v(495.7, 4.99) * mm});
            skArc(sketch, "E15.32.0.3", {"start": v(498.18, 10.16) * mm, "mid": v(497.73, 10.02) * mm, "end": v(497.45, 9.65) * mm});
            skLineSegment(sketch, "E15.32.0.4", {"start": v(498.18, 10.16) * mm, "end": v(500.04, 10.16) * mm});
            skArc(sketch, "E15.32.0.5", {"start": v(500.77, 9.65) * mm, "mid": v(500.49, 10.02) * mm, "end": v(500.04, 10.16) * mm});
            skLineSegment(sketch, "E15.32.0.6", {"start": v(500.77, 9.65) * mm, "end": v(502.52, 4.99) * mm});
            skArc(sketch, "E15.32.0.7", {"start": v(502.92, 2.76) * mm, "mid": v(502.82, 3.9) * mm, "end": v(502.52, 4.99) * mm});
            skLineSegment(sketch, "E15.32.0.8", {"start": v(502.92, 0) * mm, "end": v(502.92, 2.76) * mm});
            skLineSegment(sketch, "E15.33.0.0", {"start": v(510.54, 0) * mm, "end": v(510.54, 2.76) * mm});
            skArc(sketch, "E15.33.0.1", {"start": v(510.94, 4.99) * mm, "mid": v(510.64, 3.9) * mm, "end": v(510.54, 2.76) * mm});
            skLineSegment(sketch, "E15.33.0.2", {"start": v(512.69, 9.65) * mm, "end": v(510.94, 4.99) * mm});
            skArc(sketch, "E15.33.0.3", {"start": v(513.42, 10.16) * mm, "mid": v(512.97, 10.02) * mm, "end": v(512.69, 9.65) * mm});
            skLineSegment(sketch, "E15.33.0.4", {"start": v(513.42, 10.16) * mm, "end": v(515.28, 10.16) * mm});
            skArc(sketch, "E15.33.0.5", {"start": v(516.01, 9.65) * mm, "mid": v(515.73, 10.02) * mm, "end": v(515.28, 10.16) * mm});
            skLineSegment(sketch, "E15.33.0.6", {"start": v(516.01, 9.65) * mm, "end": v(517.76, 4.99) * mm});
            skArc(sketch, "E15.33.0.7", {"start": v(518.16, 2.76) * mm, "mid": v(518.06, 3.9) * mm, "end": v(517.76, 4.99) * mm});
            skLineSegment(sketch, "E15.33.0.8", {"start": v(518.16, 0) * mm, "end": v(518.16, 2.76) * mm});
            skLineSegment(sketch, "E15.34.0.0", {"start": v(525.78, 0) * mm, "end": v(525.78, 2.76) * mm});
            skArc(sketch, "E15.34.0.1", {"start": v(526.18, 4.99) * mm, "mid": v(525.88, 3.9) * mm, "end": v(525.78, 2.76) * mm});
            skLineSegment(sketch, "E15.34.0.2", {"start": v(527.93, 9.65) * mm, "end": v(526.18, 4.99) * mm});
            skArc(sketch, "E15.34.0.3", {"start": v(528.66, 10.16) * mm, "mid": v(528.21, 10.02) * mm, "end": v(527.93, 9.65) * mm});
            skLineSegment(sketch, "E15.34.0.4", {"start": v(528.66, 10.16) * mm, "end": v(530.52, 10.16) * mm});
            skArc(sketch, "E15.34.0.5", {"start": v(531.25, 9.65) * mm, "mid": v(530.97, 10.02) * mm, "end": v(530.52, 10.16) * mm});
            skLineSegment(sketch, "E15.34.0.6", {"start": v(531.25, 9.65) * mm, "end": v(533, 4.99) * mm});
            skArc(sketch, "E15.34.0.7", {"start": v(533.4, 2.76) * mm, "mid": v(533.3, 3.9) * mm, "end": v(533, 4.99) * mm});
            skLineSegment(sketch, "E15.34.0.8", {"start": v(533.4, 0) * mm, "end": v(533.4, 2.76) * mm});
            skLineSegment(sketch, "E15.35.0.0", {"start": v(541.02, 0) * mm, "end": v(541.02, 2.76) * mm});
            skArc(sketch, "E15.35.0.1", {"start": v(541.42, 4.99) * mm, "mid": v(541.12, 3.9) * mm, "end": v(541.02, 2.76) * mm});
            skLineSegment(sketch, "E15.35.0.2", {"start": v(543.17, 9.65) * mm, "end": v(541.42, 4.99) * mm});
            skArc(sketch, "E15.35.0.3", {"start": v(543.9, 10.16) * mm, "mid": v(543.45, 10.02) * mm, "end": v(543.17, 9.65) * mm});
            skLineSegment(sketch, "E15.35.0.4", {"start": v(543.9, 10.16) * mm, "end": v(545.76, 10.16) * mm});
            skArc(sketch, "E15.35.0.5", {"start": v(546.5, 9.65) * mm, "mid": v(546.2, 10.02) * mm, "end": v(545.76, 10.16) * mm});
            skLineSegment(sketch, "E15.35.0.6", {"start": v(546.5, 9.65) * mm, "end": v(548.24, 4.99) * mm});
            skArc(sketch, "E15.35.0.7", {"start": v(548.64, 2.76) * mm, "mid": v(548.54, 3.9) * mm, "end": v(548.24, 4.99) * mm});
            skLineSegment(sketch, "E15.35.0.8", {"start": v(548.64, 0) * mm, "end": v(548.64, 2.76) * mm});
            skLineSegment(sketch, "E15.36.0.0", {"start": v(556.26, 0) * mm, "end": v(556.26, 2.76) * mm});
            skArc(sketch, "E15.36.0.1", {"start": v(556.66, 4.99) * mm, "mid": v(556.36, 3.9) * mm, "end": v(556.26, 2.76) * mm});
            skLineSegment(sketch, "E15.36.0.2", {"start": v(558.4, 9.65) * mm, "end": v(556.66, 4.99) * mm});
            skArc(sketch, "E15.36.0.3", {"start": v(559.14, 10.16) * mm, "mid": v(558.7, 10.02) * mm, "end": v(558.4, 9.65) * mm});
            skLineSegment(sketch, "E15.36.0.4", {"start": v(559.14, 10.16) * mm, "end": v(561, 10.16) * mm});
            skArc(sketch, "E15.36.0.5", {"start": v(561.73, 9.65) * mm, "mid": v(561.45, 10.02) * mm, "end": v(561, 10.16) * mm});
            skLineSegment(sketch, "E15.36.0.6", {"start": v(561.73, 9.65) * mm, "end": v(563.48, 4.99) * mm});
            skArc(sketch, "E15.36.0.7", {"start": v(563.88, 2.76) * mm, "mid": v(563.78, 3.9) * mm, "end": v(563.48, 4.99) * mm});
            skLineSegment(sketch, "E15.36.0.8", {"start": v(563.88, 0) * mm, "end": v(563.88, 2.76) * mm});
            skLineSegment(sketch, "E15.37.0.0", {"start": v(571.5, 0) * mm, "end": v(571.5, 2.76) * mm});
            skArc(sketch, "E15.37.0.1", {"start": v(571.9, 4.99) * mm, "mid": v(571.6, 3.9) * mm, "end": v(571.5, 2.76) * mm});
            skLineSegment(sketch, "E15.37.0.2", {"start": v(573.65, 9.65) * mm, "end": v(571.9, 4.99) * mm});
            skArc(sketch, "E15.37.0.3", {"start": v(574.38, 10.16) * mm, "mid": v(573.93, 10.02) * mm, "end": v(573.65, 9.65) * mm});
            skLineSegment(sketch, "E15.37.0.4", {"start": v(574.38, 10.16) * mm, "end": v(576.24, 10.16) * mm});
            skArc(sketch, "E15.37.0.5", {"start": v(576.97, 9.65) * mm, "mid": v(576.69, 10.02) * mm, "end": v(576.24, 10.16) * mm});
            skLineSegment(sketch, "E15.37.0.6", {"start": v(576.97, 9.65) * mm, "end": v(578.72, 4.99) * mm});
            skArc(sketch, "E15.37.0.7", {"start": v(579.12, 2.76) * mm, "mid": v(579.02, 3.9) * mm, "end": v(578.72, 4.99) * mm});
            skLineSegment(sketch, "E15.37.0.8", {"start": v(579.12, 0) * mm, "end": v(579.12, 2.76) * mm});
            skLineSegment(sketch, "E15.38.0.0", {"start": v(586.74, 0) * mm, "end": v(586.74, 2.76) * mm});
            skArc(sketch, "E15.38.0.1", {"start": v(587.14, 4.99) * mm, "mid": v(586.84, 3.9) * mm, "end": v(586.74, 2.76) * mm});
            skLineSegment(sketch, "E15.38.0.2", {"start": v(588.89, 9.65) * mm, "end": v(587.14, 4.99) * mm});
            skArc(sketch, "E15.38.0.3", {"start": v(589.62, 10.16) * mm, "mid": v(589.17, 10.02) * mm, "end": v(588.89, 9.65) * mm});
            skLineSegment(sketch, "E15.38.0.4", {"start": v(589.62, 10.16) * mm, "end": v(591.48, 10.16) * mm});
            skArc(sketch, "E15.38.0.5", {"start": v(592.21, 9.65) * mm, "mid": v(591.93, 10.02) * mm, "end": v(591.48, 10.16) * mm});
            skLineSegment(sketch, "E15.38.0.6", {"start": v(592.21, 9.65) * mm, "end": v(593.96, 4.99) * mm});
            skArc(sketch, "E15.38.0.7", {"start": v(594.36, 2.76) * mm, "mid": v(594.26, 3.9) * mm, "end": v(593.96, 4.99) * mm});
            skLineSegment(sketch, "E15.38.0.8", {"start": v(594.36, 0) * mm, "end": v(594.36, 2.76) * mm});
            skLineSegment(sketch, "E15.39.0.0", {"start": v(601.98, 0) * mm, "end": v(601.98, 2.76) * mm});
            skArc(sketch, "E15.39.0.1", {"start": v(602.38, 4.99) * mm, "mid": v(602.08, 3.9) * mm, "end": v(601.98, 2.76) * mm});
            skLineSegment(sketch, "E15.39.0.2", {"start": v(604.13, 9.65) * mm, "end": v(602.38, 4.99) * mm});
            skArc(sketch, "E15.39.0.3", {"start": v(604.86, 10.16) * mm, "mid": v(604.41, 10.02) * mm, "end": v(604.13, 9.65) * mm});
            skLineSegment(sketch, "E15.39.0.4", {"start": v(604.86, 10.16) * mm, "end": v(606.72, 10.16) * mm});
            skArc(sketch, "E15.39.0.5", {"start": v(607.45, 9.65) * mm, "mid": v(607.17, 10.02) * mm, "end": v(606.72, 10.16) * mm});
            skLineSegment(sketch, "E15.39.0.6", {"start": v(607.45, 9.65) * mm, "end": v(609.2, 4.99) * mm});
            skArc(sketch, "E15.39.0.7", {"start": v(609.6, 2.76) * mm, "mid": v(609.5, 3.9) * mm, "end": v(609.2, 4.99) * mm});
            skLineSegment(sketch, "E15.39.0.8", {"start": v(609.6, 0) * mm, "end": v(609.6, 2.76) * mm});
            skLineSegment(sketch, "E15.40.0.0", {"start": v(617.22, 0) * mm, "end": v(617.22, 2.76) * mm});
            skArc(sketch, "E15.40.0.1", {"start": v(617.62, 4.99) * mm, "mid": v(617.32, 3.9) * mm, "end": v(617.22, 2.76) * mm});
            skLineSegment(sketch, "E15.40.0.2", {"start": v(619.37, 9.65) * mm, "end": v(617.62, 4.99) * mm});
            skArc(sketch, "E15.40.0.3", {"start": v(620.1, 10.16) * mm, "mid": v(619.65, 10.02) * mm, "end": v(619.37, 9.65) * mm});
            skLineSegment(sketch, "E15.40.0.4", {"start": v(620.1, 10.16) * mm, "end": v(621.96, 10.16) * mm});
            skArc(sketch, "E15.40.0.5", {"start": v(622.7, 9.65) * mm, "mid": v(622.4, 10.02) * mm, "end": v(621.96, 10.16) * mm});
            skLineSegment(sketch, "E15.40.0.6", {"start": v(622.7, 9.65) * mm, "end": v(624.44, 4.99) * mm});
            skArc(sketch, "E15.40.0.7", {"start": v(624.84, 2.76) * mm, "mid": v(624.74, 3.9) * mm, "end": v(624.44, 4.99) * mm});
            skLineSegment(sketch, "E15.40.0.8", {"start": v(624.84, 0) * mm, "end": v(624.84, 2.76) * mm});
            skLineSegment(sketch, "E15.41.0.0", {"start": v(632.46, 0) * mm, "end": v(632.46, 2.76) * mm});
            skArc(sketch, "E15.41.0.1", {"start": v(632.86, 4.99) * mm, "mid": v(632.56, 3.9) * mm, "end": v(632.46, 2.76) * mm});
            skLineSegment(sketch, "E15.41.0.2", {"start": v(634.6, 9.65) * mm, "end": v(632.86, 4.99) * mm});
            skArc(sketch, "E15.41.0.3", {"start": v(635.34, 10.16) * mm, "mid": v(634.9, 10.02) * mm, "end": v(634.6, 9.65) * mm});
            skLineSegment(sketch, "E15.41.0.4", {"start": v(635.34, 10.16) * mm, "end": v(637.2, 10.16) * mm});
            skArc(sketch, "E15.41.0.5", {"start": v(637.93, 9.65) * mm, "mid": v(637.65, 10.02) * mm, "end": v(637.2, 10.16) * mm});
            skLineSegment(sketch, "E15.41.0.6", {"start": v(637.93, 9.65) * mm, "end": v(639.68, 4.99) * mm});
            skArc(sketch, "E15.41.0.7", {"start": v(640.08, 2.76) * mm, "mid": v(639.98, 3.9) * mm, "end": v(639.68, 4.99) * mm});
            skLineSegment(sketch, "E15.41.0.8", {"start": v(640.08, 0) * mm, "end": v(640.08, 2.76) * mm});
            skLineSegment(sketch, "E15.42.0.0", {"start": v(647.7, 0) * mm, "end": v(647.7, 2.76) * mm});
            skArc(sketch, "E15.42.0.1", {"start": v(648.1, 4.99) * mm, "mid": v(647.8, 3.9) * mm, "end": v(647.7, 2.76) * mm});
            skLineSegment(sketch, "E15.42.0.2", {"start": v(649.85, 9.65) * mm, "end": v(648.1, 4.99) * mm});
            skArc(sketch, "E15.42.0.3", {"start": v(650.58, 10.16) * mm, "mid": v(650.13, 10.02) * mm, "end": v(649.85, 9.65) * mm});
            skLineSegment(sketch, "E15.42.0.4", {"start": v(650.58, 10.16) * mm, "end": v(652.44, 10.16) * mm});
            skArc(sketch, "E15.42.0.5", {"start": v(653.17, 9.65) * mm, "mid": v(652.89, 10.02) * mm, "end": v(652.44, 10.16) * mm});
            skLineSegment(sketch, "E15.42.0.6", {"start": v(653.17, 9.65) * mm, "end": v(654.92, 4.99) * mm});
            skArc(sketch, "E15.42.0.7", {"start": v(655.32, 2.76) * mm, "mid": v(655.22, 3.9) * mm, "end": v(654.92, 4.99) * mm});
            skLineSegment(sketch, "E15.42.0.8", {"start": v(655.32, 0) * mm, "end": v(655.32, 2.76) * mm});
            skLineSegment(sketch, "E15.43.0.0", {"start": v(662.94, 0) * mm, "end": v(662.94, 2.76) * mm});
            skArc(sketch, "E15.43.0.1", {"start": v(663.34, 4.99) * mm, "mid": v(663.04, 3.9) * mm, "end": v(662.94, 2.76) * mm});
            skLineSegment(sketch, "E15.43.0.2", {"start": v(665.09, 9.65) * mm, "end": v(663.34, 4.99) * mm});
            skArc(sketch, "E15.43.0.3", {"start": v(665.82, 10.16) * mm, "mid": v(665.37, 10.02) * mm, "end": v(665.09, 9.65) * mm});
            skLineSegment(sketch, "E15.43.0.4", {"start": v(665.82, 10.16) * mm, "end": v(667.68, 10.16) * mm});
            skArc(sketch, "E15.43.0.5", {"start": v(668.41, 9.65) * mm, "mid": v(668.13, 10.02) * mm, "end": v(667.68, 10.16) * mm});
            skLineSegment(sketch, "E15.43.0.6", {"start": v(668.41, 9.65) * mm, "end": v(670.16, 4.99) * mm});
            skArc(sketch, "E15.43.0.7", {"start": v(670.56, 2.76) * mm, "mid": v(670.46, 3.9) * mm, "end": v(670.16, 4.99) * mm});
            skLineSegment(sketch, "E15.43.0.8", {"start": v(670.56, 0) * mm, "end": v(670.56, 2.76) * mm});
            skLineSegment(sketch, "E15.44.0.0", {"start": v(678.18, 0) * mm, "end": v(678.18, 2.76) * mm});
            skArc(sketch, "E15.44.0.1", {"start": v(678.58, 4.99) * mm, "mid": v(678.28, 3.9) * mm, "end": v(678.18, 2.76) * mm});
            skLineSegment(sketch, "E15.44.0.2", {"start": v(680.33, 9.65) * mm, "end": v(678.58, 4.99) * mm});
            skArc(sketch, "E15.44.0.3", {"start": v(681.06, 10.16) * mm, "mid": v(680.61, 10.02) * mm, "end": v(680.33, 9.65) * mm});
            skLineSegment(sketch, "E15.44.0.4", {"start": v(681.06, 10.16) * mm, "end": v(682.92, 10.16) * mm});
            skArc(sketch, "E15.44.0.5", {"start": v(683.65, 9.65) * mm, "mid": v(683.37, 10.02) * mm, "end": v(682.92, 10.16) * mm});
            skLineSegment(sketch, "E15.44.0.6", {"start": v(683.65, 9.65) * mm, "end": v(685.4, 4.99) * mm});
            skArc(sketch, "E15.44.0.7", {"start": v(685.8, 2.76) * mm, "mid": v(685.7, 3.9) * mm, "end": v(685.4, 4.99) * mm});
            skLineSegment(sketch, "E15.44.0.8", {"start": v(685.8, 0) * mm, "end": v(685.8, 2.76) * mm});
            skLineSegment(sketch, "E15.45.0.0", {"start": v(693.42, 0) * mm, "end": v(693.42, 2.76) * mm});
            skArc(sketch, "E15.45.0.1", {"start": v(693.82, 4.99) * mm, "mid": v(693.52, 3.9) * mm, "end": v(693.42, 2.76) * mm});
            skLineSegment(sketch, "E15.45.0.2", {"start": v(695.57, 9.65) * mm, "end": v(693.82, 4.99) * mm});
            skArc(sketch, "E15.45.0.3", {"start": v(696.3, 10.16) * mm, "mid": v(695.85, 10.02) * mm, "end": v(695.57, 9.65) * mm});
            skLineSegment(sketch, "E15.45.0.4", {"start": v(696.3, 10.16) * mm, "end": v(698.16, 10.16) * mm});
            skArc(sketch, "E15.45.0.5", {"start": v(698.9, 9.65) * mm, "mid": v(698.6, 10.02) * mm, "end": v(698.16, 10.16) * mm});
            skLineSegment(sketch, "E15.45.0.6", {"start": v(698.9, 9.65) * mm, "end": v(700.64, 4.99) * mm});
            skArc(sketch, "E15.45.0.7", {"start": v(701.04, 2.76) * mm, "mid": v(700.94, 3.9) * mm, "end": v(700.64, 4.99) * mm});
            skLineSegment(sketch, "E15.45.0.8", {"start": v(701.04, 0) * mm, "end": v(701.04, 2.76) * mm});
            skLineSegment(sketch, "E15.46.0.0", {"start": v(708.66, 0) * mm, "end": v(708.66, 2.76) * mm});
            skArc(sketch, "E15.46.0.1", {"start": v(709.06, 4.99) * mm, "mid": v(708.76, 3.9) * mm, "end": v(708.66, 2.76) * mm});
            skLineSegment(sketch, "E15.46.0.2", {"start": v(710.8, 9.65) * mm, "end": v(709.06, 4.99) * mm});
            skArc(sketch, "E15.46.0.3", {"start": v(711.54, 10.16) * mm, "mid": v(711.1, 10.02) * mm, "end": v(710.8, 9.65) * mm});
            skLineSegment(sketch, "E15.46.0.4", {"start": v(711.54, 10.16) * mm, "end": v(713.4, 10.16) * mm});
            skArc(sketch, "E15.46.0.5", {"start": v(714.13, 9.65) * mm, "mid": v(713.85, 10.02) * mm, "end": v(713.4, 10.16) * mm});
            skLineSegment(sketch, "E15.46.0.6", {"start": v(714.13, 9.65) * mm, "end": v(715.88, 4.99) * mm});
            skArc(sketch, "E15.46.0.7", {"start": v(716.28, 2.76) * mm, "mid": v(716.18, 3.9) * mm, "end": v(715.88, 4.99) * mm});
            skLineSegment(sketch, "E15.46.0.8", {"start": v(716.28, 0) * mm, "end": v(716.28, 2.76) * mm});
            skLineSegment(sketch, "E15.47.0.0", {"start": v(723.9, 0) * mm, "end": v(723.9, 2.76) * mm});
            skArc(sketch, "E15.47.0.1", {"start": v(724.3, 4.99) * mm, "mid": v(724, 3.9) * mm, "end": v(723.9, 2.76) * mm});
            skLineSegment(sketch, "E15.47.0.2", {"start": v(726.05, 9.65) * mm, "end": v(724.3, 4.99) * mm});
            skArc(sketch, "E15.47.0.3", {"start": v(726.78, 10.16) * mm, "mid": v(726.33, 10.02) * mm, "end": v(726.05, 9.65) * mm});
            skLineSegment(sketch, "E15.47.0.4", {"start": v(726.78, 10.16) * mm, "end": v(728.64, 10.16) * mm});
            skArc(sketch, "E15.47.0.5", {"start": v(729.37, 9.65) * mm, "mid": v(729.09, 10.02) * mm, "end": v(728.64, 10.16) * mm});
            skLineSegment(sketch, "E15.47.0.6", {"start": v(729.37, 9.65) * mm, "end": v(731.12, 4.99) * mm});
            skArc(sketch, "E15.47.0.7", {"start": v(731.52, 2.76) * mm, "mid": v(731.42, 3.9) * mm, "end": v(731.12, 4.99) * mm});
            skLineSegment(sketch, "E15.47.0.8", {"start": v(731.52, 0) * mm, "end": v(731.52, 2.76) * mm});
            skLineSegment(sketch, "E15.48.0.0", {"start": v(739.14, 0) * mm, "end": v(739.14, 2.76) * mm});
            skArc(sketch, "E15.48.0.1", {"start": v(739.54, 4.99) * mm, "mid": v(739.24, 3.9) * mm, "end": v(739.14, 2.76) * mm});
            skLineSegment(sketch, "E15.48.0.2", {"start": v(741.29, 9.65) * mm, "end": v(739.54, 4.99) * mm});
            skArc(sketch, "E15.48.0.3", {"start": v(742.02, 10.16) * mm, "mid": v(741.57, 10.02) * mm, "end": v(741.29, 9.65) * mm});
            skLineSegment(sketch, "E15.48.0.4", {"start": v(742.02, 10.16) * mm, "end": v(743.88, 10.16) * mm});
            skArc(sketch, "E15.48.0.5", {"start": v(744.61, 9.65) * mm, "mid": v(744.33, 10.02) * mm, "end": v(743.88, 10.16) * mm});
            skLineSegment(sketch, "E15.48.0.6", {"start": v(744.61, 9.65) * mm, "end": v(746.36, 4.99) * mm});
            skArc(sketch, "E15.48.0.7", {"start": v(746.76, 2.76) * mm, "mid": v(746.66, 3.9) * mm, "end": v(746.36, 4.99) * mm});
            skLineSegment(sketch, "E15.48.0.8", {"start": v(746.76, 0) * mm, "end": v(746.76, 2.76) * mm});
            skLineSegment(sketch, "E15.49.0.0", {"start": v(754.38, 0) * mm, "end": v(754.38, 2.76) * mm});
            skArc(sketch, "E15.49.0.1", {"start": v(754.78, 4.99) * mm, "mid": v(754.48, 3.9) * mm, "end": v(754.38, 2.76) * mm});
            skLineSegment(sketch, "E15.49.0.2", {"start": v(756.53, 9.65) * mm, "end": v(754.78, 4.99) * mm});
            skArc(sketch, "E15.49.0.3", {"start": v(757.26, 10.16) * mm, "mid": v(756.81, 10.02) * mm, "end": v(756.53, 9.65) * mm});
            skLineSegment(sketch, "E15.49.0.4", {"start": v(757.26, 10.16) * mm, "end": v(759.12, 10.16) * mm});
            skArc(sketch, "E15.49.0.5", {"start": v(759.85, 9.65) * mm, "mid": v(759.57, 10.02) * mm, "end": v(759.12, 10.16) * mm});
            skLineSegment(sketch, "E15.49.0.6", {"start": v(759.85, 9.65) * mm, "end": v(761.6, 4.99) * mm});
            skArc(sketch, "E15.49.0.7", {"start": v(762, 2.76) * mm, "mid": v(761.9, 3.9) * mm, "end": v(761.6, 4.99) * mm});
            skLineSegment(sketch, "E15.49.0.8", {"start": v(762, 0) * mm, "end": v(762, 2.76) * mm});
            skLineSegment(sketch, "E15.direction1", {"start": v(7.62, 0) * mm, "end": v(22.86, 0) * mm, "construction": true});
            skLineSegment(sketch, "E16", {"start": v(762, 0) * mm, "end": v(762, -19.05) * mm});
            skSolve(sketch);
        }
        {
            var Q0;
            Q0=qCreatedBy(makeId("Front.planeOp"),FACE);
            var sketch = newSketch(context, id + "F1", { "sketchPlane" : qUnion([Q0])});
            skLineSegment(sketch, "E17", {"start": v(50.8, -6.35) * mm, "end": v(50.8, -19.05) * mm});
            skLineSegment(sketch, "E18", {"start": v(50.8, -19.05) * mm, "end": v(0, -19.05) * mm});
            skLineSegment(sketch, "E19", {"start": v(0, -6.35) * mm, "end": v(0, -19.05) * mm});
            skLineSegment(sketch, "E20", {"start": v(762, -6.35) * mm, "end": v(762, -19.05) * mm});
            skLineSegment(sketch, "E21", {"start": v(762, -19.05) * mm, "end": v(711.2, -19.05) * mm});
            skLineSegment(sketch, "E22", {"start": v(711.2, -19.05) * mm, "end": v(711.2, -6.35) * mm});
            skLineSegment(sketch, "E23", {"start": v(0, -6.35) * mm, "end": v(50.8, -6.35) * mm});
            skLineSegment(sketch, "E24", {"start": v(762, -6.35) * mm, "end": v(711.2, -6.35) * mm});
            skSolve(sketch);
        }
        {
            var Q0;
            Q0 = qSketchRegion(id + "F0", true);
            extrude(context, id + "F2", {"entities" : qUnion([Q0]), "depth" : 127 * mm});
        }
        {
            var Q0;
            Q0 = qSketchRegion(id + "F1", true);
            extrude(context, id + "F3", {"entities" : qUnion([Q0]), "operationType" : NewBodyOperationType.ADD, "oppositeDirection" : true, "depth" : 38.1 * mm});
        }
        {
            var Q0;
            Q0 = qSketchRegion(id + "F1", true);
            extrude(context, id + "F4", {"entities" : qUnion([Q0]), "operationType" : NewBodyOperationType.ADD, "depth" : 165.1 * mm});
        }
        {
            var Q0;
            Q0=makeQuery(id+"F4.opExtrude","CAP_EDGE",EDGE,{"disambiguationData":[OSD([sQuery(id+"F1.wireOp",EDGE,"E19")])],"isStart":false});
            var Q1;
            Q1=makeQuery(id+"F3.opExtrude","CAP_EDGE",EDGE,{"disambiguationData":[OSD([sQuery(id+"F1.wireOp",EDGE,"E19")])],"isStart":false});
            var Q2;
            Q2=makeQuery(id+"F3.opExtrude","CAP_EDGE",EDGE,{"disambiguationData":[OSD([sQuery(id+"F1.wireOp",EDGE,"E20")])],"isStart":false});
            var Q3;
            Q3=makeQuery(id+"F4.opExtrude","CAP_EDGE",EDGE,{"disambiguationData":[OSD([sQuery(id+"F1.wireOp",EDGE,"E20")])],"isStart":false});
            var Q4;
            Q4=makeQuery(id+"F4.opExtrude","CAP_EDGE",EDGE,{"disambiguationData":[OSD([sQuery(id+"F1.wireOp",EDGE,"E22")])],"isStart":false});
            var Q5;
            Q5=makeQuery(id+"F3.opExtrude","CAP_EDGE",EDGE,{"disambiguationData":[OSD([sQuery(id+"F1.wireOp",EDGE,"E22")])],"isStart":false});
            var Q6;
            Q6=makeQuery(id+"F4.opExtrude","CAP_EDGE",EDGE,{"disambiguationData":[OSD([sQuery(id+"F1.wireOp",EDGE,"E17")])],"isStart":false});
            var Q7;
            Q7=makeQuery(id+"F3.opExtrude","CAP_EDGE",EDGE,{"disambiguationData":[OSD([sQuery(id+"F1.wireOp",EDGE,"E17")])],"isStart":false});
            fillet(context, id + "F5", {"entities" : qUnion([Q0, Q1, Q2, Q3, Q4, Q5, Q6, Q7]), "radius" : 5.08 * mm, "tangentPropagation" : true, "allowEdgeOverflow" : false});
        }
        {
            var Q0;
            Q0=makeQuery(id+"F3.opExtrude","SWEPT_FACE",FACE,{"disambiguationData":[OSD([sQuery(id+"F1.wireOp",EDGE,"E23")])]});
            var sketch = newSketch(context, id + "F6", { "sketchPlane" : qUnion([Q0])});
            skPoint(sketch, "E25", {"position": v(38.1, 19.05) * mm});
            skPoint(sketch, "E26", {"position": v(12.7, 19.05) * mm});
            skPoint(sketch, "E27.MirrorP", {"position": v(12.7, -146.05) * mm});
            skPoint(sketch, "E28.MirrorP", {"position": v(38.1, -146.05) * mm});
            skPoint(sketch, "E29.MirrorP", {"position": v(723.9, -146.05) * mm});
            skPoint(sketch, "E30.MirrorP", {"position": v(749.3, -146.05) * mm});
            skPoint(sketch, "E31.MirrorP", {"position": v(749.3, 19.05) * mm});
            skPoint(sketch, "E32.MirrorP", {"position": v(723.9, 19.05) * mm});
            skSolve(sketch);
        }
        {
            var Q0;
            Q0=sQuery(id+"F6.wireOp",VERTEX,"E26");
            var Q1;
            Q1=sQuery(id+"F6.wireOp",VERTEX,"E25");
            var Q2;
            Q2=sQuery(id+"F6.wireOp",VERTEX,"E27.MirrorP");
            var Q3;
            Q3=sQuery(id+"F6.wireOp",VERTEX,"E28.MirrorP");
            var Q4;
            Q4=sQuery(id+"F6.wireOp",VERTEX,"E32.MirrorP");
            var Q5;
            Q5=sQuery(id+"F6.wireOp",VERTEX,"E31.MirrorP");
            var Q6;
            Q6=sQuery(id+"F6.wireOp",VERTEX,"E29.MirrorP");
            var Q7;
            Q7=sQuery(id+"F6.wireOp",VERTEX,"E30.MirrorP");
            var Q8;
            Q8=makeQuery(id+"F2.opExtrude","SWEPT_BODY",BODY,{"disambiguationData":[OSD([sQuery(id+"F0.wireOp",EDGE,"E0"),sQuery(id+"F0.wireOp",EDGE,"E1"),sQuery(id+"F0.wireOp",EDGE,"E3"),sQuery(id+"F0.wireOp",EDGE,"E4"),sQuery(id+"F0.wireOp",EDGE,"E5"),sQuery(id+"F0.wireOp",EDGE,"E6"),sQuery(id+"F0.wireOp",EDGE,"E7.filletArc"),sQuery(id+"F0.wireOp",EDGE,"E8.filletArc"),sQuery(id+"F0.wireOp",EDGE,"E9.filletArc"),sQuery(id+"F0.wireOp",EDGE,"E10.filletArc"),sQuery(id+"F0.wireOp",EDGE,"E11"),sQuery(id+"F0.wireOp",EDGE,"E12"),sQuery(id+"F0.wireOp",EDGE,"E13"),sQuery(id+"F0.wireOp",EDGE,"E14"),sQuery(id+"F0.wireOp",EDGE,"E15.1.0.0"),sQuery(id+"F0.wireOp",EDGE,"E15.1.0.1"),sQuery(id+"F0.wireOp",EDGE,"E15.1.0.2"),sQuery(id+"F0.wireOp",EDGE,"E15.1.0.3"),sQuery(id+"F0.wireOp",EDGE,"E15.1.0.4"),sQuery(id+"F0.wireOp",EDGE,"E15.1.0.5"),sQuery(id+"F0.wireOp",EDGE,"E15.1.0.6"),sQuery(id+"F0.wireOp",EDGE,"E15.1.0.7"),sQuery(id+"F0.wireOp",EDGE,"E15.1.0.8"),sQuery(id+"F0.wireOp",EDGE,"E15.2.0.0"),sQuery(id+"F0.wireOp",EDGE,"E15.2.0.1"),sQuery(id+"F0.wireOp",EDGE,"E15.2.0.2"),sQuery(id+"F0.wireOp",EDGE,"E15.2.0.3"),sQuery(id+"F0.wireOp",EDGE,"E15.2.0.4"),sQuery(id+"F0.wireOp",EDGE,"E15.2.0.5"),sQuery(id+"F0.wireOp",EDGE,"E15.2.0.6"),sQuery(id+"F0.wireOp",EDGE,"E15.2.0.7"),sQuery(id+"F0.wireOp",EDGE,"E15.2.0.8"),sQuery(id+"F0.wireOp",EDGE,"E15.3.0.0"),sQuery(id+"F0.wireOp",EDGE,"E15.3.0.1"),sQuery(id+"F0.wireOp",EDGE,"E15.3.0.2"),sQuery(id+"F0.wireOp",EDGE,"E15.3.0.3"),sQuery(id+"F0.wireOp",EDGE,"E15.3.0.4"),sQuery(id+"F0.wireOp",EDGE,"E15.3.0.5"),sQuery(id+"F0.wireOp",EDGE,"E15.3.0.6"),sQuery(id+"F0.wireOp",EDGE,"E15.3.0.7"),sQuery(id+"F0.wireOp",EDGE,"E15.3.0.8"),sQuery(id+"F0.wireOp",EDGE,"E15.4.0.0"),sQuery(id+"F0.wireOp",EDGE,"E15.4.0.1"),sQuery(id+"F0.wireOp",EDGE,"E15.4.0.2"),sQuery(id+"F0.wireOp",EDGE,"E15.4.0.3"),sQuery(id+"F0.wireOp",EDGE,"E15.4.0.4"),sQuery(id+"F0.wireOp",EDGE,"E15.4.0.5"),sQuery(id+"F0.wireOp",EDGE,"E15.4.0.6"),sQuery(id+"F0.wireOp",EDGE,"E15.4.0.7"),sQuery(id+"F0.wireOp",EDGE,"E15.4.0.8"),sQuery(id+"F0.wireOp",EDGE,"E15.5.0.0"),sQuery(id+"F0.wireOp",EDGE,"E15.5.0.1"),sQuery(id+"F0.wireOp",EDGE,"E15.5.0.2"),sQuery(id+"F0.wireOp",EDGE,"E15.5.0.3"),sQuery(id+"F0.wireOp",EDGE,"E15.5.0.4"),sQuery(id+"F0.wireOp",EDGE,"E15.5.0.5"),sQuery(id+"F0.wireOp",EDGE,"E15.5.0.6"),sQuery(id+"F0.wireOp",EDGE,"E15.5.0.7"),sQuery(id+"F0.wireOp",EDGE,"E15.5.0.8"),sQuery(id+"F0.wireOp",EDGE,"E15.6.0.0"),sQuery(id+"F0.wireOp",EDGE,"E15.6.0.1"),sQuery(id+"F0.wireOp",EDGE,"E15.6.0.2"),sQuery(id+"F0.wireOp",EDGE,"E15.6.0.3"),sQuery(id+"F0.wireOp",EDGE,"E15.6.0.4"),sQuery(id+"F0.wireOp",EDGE,"E15.6.0.5"),sQuery(id+"F0.wireOp",EDGE,"E15.6.0.6"),sQuery(id+"F0.wireOp",EDGE,"E15.6.0.7"),sQuery(id+"F0.wireOp",EDGE,"E15.6.0.8"),sQuery(id+"F0.wireOp",EDGE,"E15.7.0.0"),sQuery(id+"F0.wireOp",EDGE,"E15.7.0.1"),sQuery(id+"F0.wireOp",EDGE,"E15.7.0.2"),sQuery(id+"F0.wireOp",EDGE,"E15.7.0.3"),sQuery(id+"F0.wireOp",EDGE,"E15.7.0.4"),sQuery(id+"F0.wireOp",EDGE,"E15.7.0.5"),sQuery(id+"F0.wireOp",EDGE,"E15.7.0.6"),sQuery(id+"F0.wireOp",EDGE,"E15.7.0.7"),sQuery(id+"F0.wireOp",EDGE,"E15.7.0.8"),sQuery(id+"F0.wireOp",EDGE,"E15.8.0.0"),sQuery(id+"F0.wireOp",EDGE,"E15.8.0.1"),sQuery(id+"F0.wireOp",EDGE,"E15.8.0.2"),sQuery(id+"F0.wireOp",EDGE,"E15.8.0.3"),sQuery(id+"F0.wireOp",EDGE,"E15.8.0.4"),sQuery(id+"F0.wireOp",EDGE,"E15.8.0.5"),sQuery(id+"F0.wireOp",EDGE,"E15.8.0.6"),sQuery(id+"F0.wireOp",EDGE,"E15.8.0.7"),sQuery(id+"F0.wireOp",EDGE,"E15.8.0.8"),sQuery(id+"F0.wireOp",EDGE,"E15.9.0.0"),sQuery(id+"F0.wireOp",EDGE,"E15.9.0.1"),sQuery(id+"F0.wireOp",EDGE,"E15.9.0.2"),sQuery(id+"F0.wireOp",EDGE,"E15.9.0.3"),sQuery(id+"F0.wireOp",EDGE,"E15.9.0.4"),sQuery(id+"F0.wireOp",EDGE,"E15.9.0.5"),sQuery(id+"F0.wireOp",EDGE,"E15.9.0.6"),sQuery(id+"F0.wireOp",EDGE,"E15.9.0.7"),sQuery(id+"F0.wireOp",EDGE,"E15.9.0.8"),sQuery(id+"F0.wireOp",EDGE,"E15.10.0.0"),sQuery(id+"F0.wireOp",EDGE,"E15.10.0.1"),sQuery(id+"F0.wireOp",EDGE,"E15.10.0.2"),sQuery(id+"F0.wireOp",EDGE,"E15.10.0.3"),sQuery(id+"F0.wireOp",EDGE,"E15.10.0.4"),sQuery(id+"F0.wireOp",EDGE,"E15.10.0.5"),sQuery(id+"F0.wireOp",EDGE,"E15.10.0.6"),sQuery(id+"F0.wireOp",EDGE,"E15.10.0.7"),sQuery(id+"F0.wireOp",EDGE,"E15.10.0.8"),sQuery(id+"F0.wireOp",EDGE,"E15.11.0.0"),sQuery(id+"F0.wireOp",EDGE,"E15.11.0.1"),sQuery(id+"F0.wireOp",EDGE,"E15.11.0.2"),sQuery(id+"F0.wireOp",EDGE,"E15.11.0.3"),sQuery(id+"F0.wireOp",EDGE,"E15.11.0.4"),sQuery(id+"F0.wireOp",EDGE,"E15.11.0.5"),sQuery(id+"F0.wireOp",EDGE,"E15.11.0.6"),sQuery(id+"F0.wireOp",EDGE,"E15.11.0.7"),sQuery(id+"F0.wireOp",EDGE,"E15.11.0.8"),sQuery(id+"F0.wireOp",EDGE,"E15.12.0.0"),sQuery(id+"F0.wireOp",EDGE,"E15.12.0.1"),sQuery(id+"F0.wireOp",EDGE,"E15.12.0.2"),sQuery(id+"F0.wireOp",EDGE,"E15.12.0.3"),sQuery(id+"F0.wireOp",EDGE,"E15.12.0.4"),sQuery(id+"F0.wireOp",EDGE,"E15.12.0.5"),sQuery(id+"F0.wireOp",EDGE,"E15.12.0.6"),sQuery(id+"F0.wireOp",EDGE,"E15.12.0.7"),sQuery(id+"F0.wireOp",EDGE,"E15.12.0.8"),sQuery(id+"F0.wireOp",EDGE,"E15.13.0.0"),sQuery(id+"F0.wireOp",EDGE,"E15.13.0.1"),sQuery(id+"F0.wireOp",EDGE,"E15.13.0.2"),sQuery(id+"F0.wireOp",EDGE,"E15.13.0.3"),sQuery(id+"F0.wireOp",EDGE,"E15.13.0.4"),sQuery(id+"F0.wireOp",EDGE,"E15.13.0.5"),sQuery(id+"F0.wireOp",EDGE,"E15.13.0.6"),sQuery(id+"F0.wireOp",EDGE,"E15.13.0.7"),sQuery(id+"F0.wireOp",EDGE,"E15.13.0.8"),sQuery(id+"F0.wireOp",EDGE,"E15.14.0.0"),sQuery(id+"F0.wireOp",EDGE,"E15.14.0.1"),sQuery(id+"F0.wireOp",EDGE,"E15.14.0.2"),sQuery(id+"F0.wireOp",EDGE,"E15.14.0.3"),sQuery(id+"F0.wireOp",EDGE,"E15.14.0.4"),sQuery(id+"F0.wireOp",EDGE,"E15.14.0.5"),sQuery(id+"F0.wireOp",EDGE,"E15.14.0.6"),sQuery(id+"F0.wireOp",EDGE,"E15.14.0.7"),sQuery(id+"F0.wireOp",EDGE,"E15.14.0.8"),sQuery(id+"F0.wireOp",EDGE,"E15.15.0.0"),sQuery(id+"F0.wireOp",EDGE,"E15.15.0.1"),sQuery(id+"F0.wireOp",EDGE,"E15.15.0.2"),sQuery(id+"F0.wireOp",EDGE,"E15.15.0.3"),sQuery(id+"F0.wireOp",EDGE,"E15.15.0.4"),sQuery(id+"F0.wireOp",EDGE,"E15.15.0.5"),sQuery(id+"F0.wireOp",EDGE,"E15.15.0.6"),sQuery(id+"F0.wireOp",EDGE,"E15.15.0.7"),sQuery(id+"F0.wireOp",EDGE,"E15.15.0.8"),sQuery(id+"F0.wireOp",EDGE,"E15.16.0.0"),sQuery(id+"F0.wireOp",EDGE,"E15.16.0.1"),sQuery(id+"F0.wireOp",EDGE,"E15.16.0.2"),sQuery(id+"F0.wireOp",EDGE,"E15.16.0.3"),sQuery(id+"F0.wireOp",EDGE,"E15.16.0.4"),sQuery(id+"F0.wireOp",EDGE,"E15.16.0.5"),sQuery(id+"F0.wireOp",EDGE,"E15.16.0.6"),sQuery(id+"F0.wireOp",EDGE,"E15.16.0.7"),sQuery(id+"F0.wireOp",EDGE,"E15.16.0.8"),sQuery(id+"F0.wireOp",EDGE,"E15.17.0.0"),sQuery(id+"F0.wireOp",EDGE,"E15.17.0.1"),sQuery(id+"F0.wireOp",EDGE,"E15.17.0.2"),sQuery(id+"F0.wireOp",EDGE,"E15.17.0.3"),sQuery(id+"F0.wireOp",EDGE,"E15.17.0.4"),sQuery(id+"F0.wireOp",EDGE,"E15.17.0.5"),sQuery(id+"F0.wireOp",EDGE,"E15.17.0.6"),sQuery(id+"F0.wireOp",EDGE,"E15.17.0.7"),sQuery(id+"F0.wireOp",EDGE,"E15.17.0.8"),sQuery(id+"F0.wireOp",EDGE,"E15.18.0.0"),sQuery(id+"F0.wireOp",EDGE,"E15.18.0.1"),sQuery(id+"F0.wireOp",EDGE,"E15.18.0.2"),sQuery(id+"F0.wireOp",EDGE,"E15.18.0.3"),sQuery(id+"F0.wireOp",EDGE,"E15.18.0.4"),sQuery(id+"F0.wireOp",EDGE,"E15.18.0.5"),sQuery(id+"F0.wireOp",EDGE,"E15.18.0.6"),sQuery(id+"F0.wireOp",EDGE,"E15.18.0.7"),sQuery(id+"F0.wireOp",EDGE,"E15.18.0.8"),sQuery(id+"F0.wireOp",EDGE,"E15.19.0.0"),sQuery(id+"F0.wireOp",EDGE,"E15.19.0.1"),sQuery(id+"F0.wireOp",EDGE,"E15.19.0.2"),sQuery(id+"F0.wireOp",EDGE,"E15.19.0.3"),sQuery(id+"F0.wireOp",EDGE,"E15.19.0.4"),sQuery(id+"F0.wireOp",EDGE,"E15.19.0.5"),sQuery(id+"F0.wireOp",EDGE,"E15.19.0.6"),sQuery(id+"F0.wireOp",EDGE,"E15.19.0.7"),sQuery(id+"F0.wireOp",EDGE,"E15.19.0.8"),sQuery(id+"F0.wireOp",EDGE,"E15.20.0.0"),sQuery(id+"F0.wireOp",EDGE,"E15.20.0.1"),sQuery(id+"F0.wireOp",EDGE,"E15.20.0.2"),sQuery(id+"F0.wireOp",EDGE,"E15.20.0.3"),sQuery(id+"F0.wireOp",EDGE,"E15.20.0.4"),sQuery(id+"F0.wireOp",EDGE,"E15.20.0.5"),sQuery(id+"F0.wireOp",EDGE,"E15.20.0.6"),sQuery(id+"F0.wireOp",EDGE,"E15.20.0.7"),sQuery(id+"F0.wireOp",EDGE,"E15.20.0.8"),sQuery(id+"F0.wireOp",EDGE,"E15.21.0.0"),sQuery(id+"F0.wireOp",EDGE,"E15.21.0.1"),sQuery(id+"F0.wireOp",EDGE,"E15.21.0.2"),sQuery(id+"F0.wireOp",EDGE,"E15.21.0.3"),sQuery(id+"F0.wireOp",EDGE,"E15.21.0.4"),sQuery(id+"F0.wireOp",EDGE,"E15.21.0.5"),sQuery(id+"F0.wireOp",EDGE,"E15.21.0.6"),sQuery(id+"F0.wireOp",EDGE,"E15.21.0.7"),sQuery(id+"F0.wireOp",EDGE,"E15.21.0.8"),sQuery(id+"F0.wireOp",EDGE,"E15.22.0.0"),sQuery(id+"F0.wireOp",EDGE,"E15.22.0.1"),sQuery(id+"F0.wireOp",EDGE,"E15.22.0.2"),sQuery(id+"F0.wireOp",EDGE,"E15.22.0.3"),sQuery(id+"F0.wireOp",EDGE,"E15.22.0.4"),sQuery(id+"F0.wireOp",EDGE,"E15.22.0.5"),sQuery(id+"F0.wireOp",EDGE,"E15.22.0.6"),sQuery(id+"F0.wireOp",EDGE,"E15.22.0.7"),sQuery(id+"F0.wireOp",EDGE,"E15.22.0.8"),sQuery(id+"F0.wireOp",EDGE,"E15.23.0.0"),sQuery(id+"F0.wireOp",EDGE,"E15.23.0.1"),sQuery(id+"F0.wireOp",EDGE,"E15.23.0.2"),sQuery(id+"F0.wireOp",EDGE,"E15.23.0.3"),sQuery(id+"F0.wireOp",EDGE,"E15.23.0.4"),sQuery(id+"F0.wireOp",EDGE,"E15.23.0.5"),sQuery(id+"F0.wireOp",EDGE,"E15.23.0.6"),sQuery(id+"F0.wireOp",EDGE,"E15.23.0.7"),sQuery(id+"F0.wireOp",EDGE,"E15.23.0.8"),sQuery(id+"F0.wireOp",EDGE,"E15.24.0.0"),sQuery(id+"F0.wireOp",EDGE,"E15.24.0.1"),sQuery(id+"F0.wireOp",EDGE,"E15.24.0.2"),sQuery(id+"F0.wireOp",EDGE,"E15.24.0.3"),sQuery(id+"F0.wireOp",EDGE,"E15.24.0.4"),sQuery(id+"F0.wireOp",EDGE,"E15.24.0.5"),sQuery(id+"F0.wireOp",EDGE,"E15.24.0.6"),sQuery(id+"F0.wireOp",EDGE,"E15.24.0.7"),sQuery(id+"F0.wireOp",EDGE,"E15.24.0.8"),sQuery(id+"F0.wireOp",EDGE,"E15.25.0.0"),sQuery(id+"F0.wireOp",EDGE,"E15.25.0.1"),sQuery(id+"F0.wireOp",EDGE,"E15.25.0.2"),sQuery(id+"F0.wireOp",EDGE,"E15.25.0.3"),sQuery(id+"F0.wireOp",EDGE,"E15.25.0.4"),sQuery(id+"F0.wireOp",EDGE,"E15.25.0.5"),sQuery(id+"F0.wireOp",EDGE,"E15.25.0.6"),sQuery(id+"F0.wireOp",EDGE,"E15.25.0.7"),sQuery(id+"F0.wireOp",EDGE,"E15.25.0.8"),sQuery(id+"F0.wireOp",EDGE,"E15.26.0.0"),sQuery(id+"F0.wireOp",EDGE,"E15.26.0.1"),sQuery(id+"F0.wireOp",EDGE,"E15.26.0.2"),sQuery(id+"F0.wireOp",EDGE,"E15.26.0.3"),sQuery(id+"F0.wireOp",EDGE,"E15.26.0.4"),sQuery(id+"F0.wireOp",EDGE,"E15.26.0.5"),sQuery(id+"F0.wireOp",EDGE,"E15.26.0.6"),sQuery(id+"F0.wireOp",EDGE,"E15.26.0.7"),sQuery(id+"F0.wireOp",EDGE,"E15.26.0.8"),sQuery(id+"F0.wireOp",EDGE,"E15.27.0.0"),sQuery(id+"F0.wireOp",EDGE,"E15.27.0.1"),sQuery(id+"F0.wireOp",EDGE,"E15.27.0.2"),sQuery(id+"F0.wireOp",EDGE,"E15.27.0.3"),sQuery(id+"F0.wireOp",EDGE,"E15.27.0.4"),sQuery(id+"F0.wireOp",EDGE,"E15.27.0.5"),sQuery(id+"F0.wireOp",EDGE,"E15.27.0.6"),sQuery(id+"F0.wireOp",EDGE,"E15.27.0.7"),sQuery(id+"F0.wireOp",EDGE,"E15.27.0.8"),sQuery(id+"F0.wireOp",EDGE,"E15.28.0.0"),sQuery(id+"F0.wireOp",EDGE,"E15.28.0.1"),sQuery(id+"F0.wireOp",EDGE,"E15.28.0.2"),sQuery(id+"F0.wireOp",EDGE,"E15.28.0.3"),sQuery(id+"F0.wireOp",EDGE,"E15.28.0.4"),sQuery(id+"F0.wireOp",EDGE,"E15.28.0.5"),sQuery(id+"F0.wireOp",EDGE,"E15.28.0.6"),sQuery(id+"F0.wireOp",EDGE,"E15.28.0.7"),sQuery(id+"F0.wireOp",EDGE,"E15.28.0.8"),sQuery(id+"F0.wireOp",EDGE,"E15.29.0.0"),sQuery(id+"F0.wireOp",EDGE,"E15.29.0.1"),sQuery(id+"F0.wireOp",EDGE,"E15.29.0.2"),sQuery(id+"F0.wireOp",EDGE,"E15.29.0.3"),sQuery(id+"F0.wireOp",EDGE,"E15.29.0.4"),sQuery(id+"F0.wireOp",EDGE,"E15.29.0.5"),sQuery(id+"F0.wireOp",EDGE,"E15.29.0.6"),sQuery(id+"F0.wireOp",EDGE,"E15.29.0.7"),sQuery(id+"F0.wireOp",EDGE,"E15.29.0.8"),sQuery(id+"F0.wireOp",EDGE,"E15.30.0.0"),sQuery(id+"F0.wireOp",EDGE,"E15.30.0.1"),sQuery(id+"F0.wireOp",EDGE,"E15.30.0.2"),sQuery(id+"F0.wireOp",EDGE,"E15.30.0.3"),sQuery(id+"F0.wireOp",EDGE,"E15.30.0.4"),sQuery(id+"F0.wireOp",EDGE,"E15.30.0.5"),sQuery(id+"F0.wireOp",EDGE,"E15.30.0.6"),sQuery(id+"F0.wireOp",EDGE,"E15.30.0.7"),sQuery(id+"F0.wireOp",EDGE,"E15.30.0.8"),sQuery(id+"F0.wireOp",EDGE,"E15.31.0.0"),sQuery(id+"F0.wireOp",EDGE,"E15.31.0.1"),sQuery(id+"F0.wireOp",EDGE,"E15.31.0.2"),sQuery(id+"F0.wireOp",EDGE,"E15.31.0.3"),sQuery(id+"F0.wireOp",EDGE,"E15.31.0.4"),sQuery(id+"F0.wireOp",EDGE,"E15.31.0.5"),sQuery(id+"F0.wireOp",EDGE,"E15.31.0.6"),sQuery(id+"F0.wireOp",EDGE,"E15.31.0.7"),sQuery(id+"F0.wireOp",EDGE,"E15.31.0.8"),sQuery(id+"F0.wireOp",EDGE,"E15.32.0.0"),sQuery(id+"F0.wireOp",EDGE,"E15.32.0.1"),sQuery(id+"F0.wireOp",EDGE,"E15.32.0.2"),sQuery(id+"F0.wireOp",EDGE,"E15.32.0.3"),sQuery(id+"F0.wireOp",EDGE,"E15.32.0.4"),sQuery(id+"F0.wireOp",EDGE,"E15.32.0.5"),sQuery(id+"F0.wireOp",EDGE,"E15.32.0.6"),sQuery(id+"F0.wireOp",EDGE,"E15.32.0.7"),sQuery(id+"F0.wireOp",EDGE,"E15.32.0.8"),sQuery(id+"F0.wireOp",EDGE,"E15.33.0.0"),sQuery(id+"F0.wireOp",EDGE,"E15.33.0.1"),sQuery(id+"F0.wireOp",EDGE,"E15.33.0.2"),sQuery(id+"F0.wireOp",EDGE,"E15.33.0.3"),sQuery(id+"F0.wireOp",EDGE,"E15.33.0.4"),sQuery(id+"F0.wireOp",EDGE,"E15.33.0.5"),sQuery(id+"F0.wireOp",EDGE,"E15.33.0.6"),sQuery(id+"F0.wireOp",EDGE,"E15.33.0.7"),sQuery(id+"F0.wireOp",EDGE,"E15.33.0.8"),sQuery(id+"F0.wireOp",EDGE,"E15.34.0.0"),sQuery(id+"F0.wireOp",EDGE,"E15.34.0.1"),sQuery(id+"F0.wireOp",EDGE,"E15.34.0.2"),sQuery(id+"F0.wireOp",EDGE,"E15.34.0.3"),sQuery(id+"F0.wireOp",EDGE,"E15.34.0.4"),sQuery(id+"F0.wireOp",EDGE,"E15.34.0.5"),sQuery(id+"F0.wireOp",EDGE,"E15.34.0.6"),sQuery(id+"F0.wireOp",EDGE,"E15.34.0.7"),sQuery(id+"F0.wireOp",EDGE,"E15.34.0.8"),sQuery(id+"F0.wireOp",EDGE,"E15.35.0.0"),sQuery(id+"F0.wireOp",EDGE,"E15.35.0.1"),sQuery(id+"F0.wireOp",EDGE,"E15.35.0.2"),sQuery(id+"F0.wireOp",EDGE,"E15.35.0.3"),sQuery(id+"F0.wireOp",EDGE,"E15.35.0.4"),sQuery(id+"F0.wireOp",EDGE,"E15.35.0.5"),sQuery(id+"F0.wireOp",EDGE,"E15.35.0.6"),sQuery(id+"F0.wireOp",EDGE,"E15.35.0.7"),sQuery(id+"F0.wireOp",EDGE,"E15.35.0.8"),sQuery(id+"F0.wireOp",EDGE,"E15.36.0.0"),sQuery(id+"F0.wireOp",EDGE,"E15.36.0.1"),sQuery(id+"F0.wireOp",EDGE,"E15.36.0.2"),sQuery(id+"F0.wireOp",EDGE,"E15.36.0.3"),sQuery(id+"F0.wireOp",EDGE,"E15.36.0.4"),sQuery(id+"F0.wireOp",EDGE,"E15.36.0.5"),sQuery(id+"F0.wireOp",EDGE,"E15.36.0.6"),sQuery(id+"F0.wireOp",EDGE,"E15.36.0.7"),sQuery(id+"F0.wireOp",EDGE,"E15.36.0.8"),sQuery(id+"F0.wireOp",EDGE,"E15.37.0.0"),sQuery(id+"F0.wireOp",EDGE,"E15.37.0.1"),sQuery(id+"F0.wireOp",EDGE,"E15.37.0.2"),sQuery(id+"F0.wireOp",EDGE,"E15.37.0.3"),sQuery(id+"F0.wireOp",EDGE,"E15.37.0.4"),sQuery(id+"F0.wireOp",EDGE,"E15.37.0.5"),sQuery(id+"F0.wireOp",EDGE,"E15.37.0.6"),sQuery(id+"F0.wireOp",EDGE,"E15.37.0.7"),sQuery(id+"F0.wireOp",EDGE,"E15.37.0.8"),sQuery(id+"F0.wireOp",EDGE,"E15.38.0.0"),sQuery(id+"F0.wireOp",EDGE,"E15.38.0.1"),sQuery(id+"F0.wireOp",EDGE,"E15.38.0.2"),sQuery(id+"F0.wireOp",EDGE,"E15.38.0.3"),sQuery(id+"F0.wireOp",EDGE,"E15.38.0.4"),sQuery(id+"F0.wireOp",EDGE,"E15.38.0.5"),sQuery(id+"F0.wireOp",EDGE,"E15.38.0.6"),sQuery(id+"F0.wireOp",EDGE,"E15.38.0.7"),sQuery(id+"F0.wireOp",EDGE,"E15.38.0.8"),sQuery(id+"F0.wireOp",EDGE,"E15.39.0.0"),sQuery(id+"F0.wireOp",EDGE,"E15.39.0.1"),sQuery(id+"F0.wireOp",EDGE,"E15.39.0.2"),sQuery(id+"F0.wireOp",EDGE,"E15.39.0.3"),sQuery(id+"F0.wireOp",EDGE,"E15.39.0.4"),sQuery(id+"F0.wireOp",EDGE,"E15.39.0.5"),sQuery(id+"F0.wireOp",EDGE,"E15.39.0.6"),sQuery(id+"F0.wireOp",EDGE,"E15.39.0.7"),sQuery(id+"F0.wireOp",EDGE,"E15.39.0.8"),sQuery(id+"F0.wireOp",EDGE,"E15.40.0.0"),sQuery(id+"F0.wireOp",EDGE,"E15.40.0.1"),sQuery(id+"F0.wireOp",EDGE,"E15.40.0.2"),sQuery(id+"F0.wireOp",EDGE,"E15.40.0.3"),sQuery(id+"F0.wireOp",EDGE,"E15.40.0.4"),sQuery(id+"F0.wireOp",EDGE,"E15.40.0.5"),sQuery(id+"F0.wireOp",EDGE,"E15.40.0.6"),sQuery(id+"F0.wireOp",EDGE,"E15.40.0.7"),sQuery(id+"F0.wireOp",EDGE,"E15.40.0.8"),sQuery(id+"F0.wireOp",EDGE,"E15.41.0.0"),sQuery(id+"F0.wireOp",EDGE,"E15.41.0.1"),sQuery(id+"F0.wireOp",EDGE,"E15.41.0.2"),sQuery(id+"F0.wireOp",EDGE,"E15.41.0.3"),sQuery(id+"F0.wireOp",EDGE,"E15.41.0.4"),sQuery(id+"F0.wireOp",EDGE,"E15.41.0.5"),sQuery(id+"F0.wireOp",EDGE,"E15.41.0.6"),sQuery(id+"F0.wireOp",EDGE,"E15.41.0.7"),sQuery(id+"F0.wireOp",EDGE,"E15.41.0.8"),sQuery(id+"F0.wireOp",EDGE,"E15.42.0.0"),sQuery(id+"F0.wireOp",EDGE,"E15.42.0.1"),sQuery(id+"F0.wireOp",EDGE,"E15.42.0.2"),sQuery(id+"F0.wireOp",EDGE,"E15.42.0.3"),sQuery(id+"F0.wireOp",EDGE,"E15.42.0.4"),sQuery(id+"F0.wireOp",EDGE,"E15.42.0.5"),sQuery(id+"F0.wireOp",EDGE,"E15.42.0.6"),sQuery(id+"F0.wireOp",EDGE,"E15.42.0.7"),sQuery(id+"F0.wireOp",EDGE,"E15.42.0.8"),sQuery(id+"F0.wireOp",EDGE,"E15.43.0.0"),sQuery(id+"F0.wireOp",EDGE,"E15.43.0.1"),sQuery(id+"F0.wireOp",EDGE,"E15.43.0.2"),sQuery(id+"F0.wireOp",EDGE,"E15.43.0.3"),sQuery(id+"F0.wireOp",EDGE,"E15.43.0.4"),sQuery(id+"F0.wireOp",EDGE,"E15.43.0.5"),sQuery(id+"F0.wireOp",EDGE,"E15.43.0.6"),sQuery(id+"F0.wireOp",EDGE,"E15.43.0.7"),sQuery(id+"F0.wireOp",EDGE,"E15.43.0.8"),sQuery(id+"F0.wireOp",EDGE,"E15.44.0.0"),sQuery(id+"F0.wireOp",EDGE,"E15.44.0.1"),sQuery(id+"F0.wireOp",EDGE,"E15.44.0.2"),sQuery(id+"F0.wireOp",EDGE,"E15.44.0.3"),sQuery(id+"F0.wireOp",EDGE,"E15.44.0.4"),sQuery(id+"F0.wireOp",EDGE,"E15.44.0.5"),sQuery(id+"F0.wireOp",EDGE,"E15.44.0.6"),sQuery(id+"F0.wireOp",EDGE,"E15.44.0.7"),sQuery(id+"F0.wireOp",EDGE,"E15.44.0.8"),sQuery(id+"F0.wireOp",EDGE,"E15.45.0.0"),sQuery(id+"F0.wireOp",EDGE,"E15.45.0.1"),sQuery(id+"F0.wireOp",EDGE,"E15.45.0.2"),sQuery(id+"F0.wireOp",EDGE,"E15.45.0.3"),sQuery(id+"F0.wireOp",EDGE,"E15.45.0.4"),sQuery(id+"F0.wireOp",EDGE,"E15.45.0.5"),sQuery(id+"F0.wireOp",EDGE,"E15.45.0.6"),sQuery(id+"F0.wireOp",EDGE,"E15.45.0.7"),sQuery(id+"F0.wireOp",EDGE,"E15.45.0.8"),sQuery(id+"F0.wireOp",EDGE,"E15.46.0.0"),sQuery(id+"F0.wireOp",EDGE,"E15.46.0.1"),sQuery(id+"F0.wireOp",EDGE,"E15.46.0.2"),sQuery(id+"F0.wireOp",EDGE,"E15.46.0.3"),sQuery(id+"F0.wireOp",EDGE,"E15.46.0.4"),sQuery(id+"F0.wireOp",EDGE,"E15.46.0.5"),sQuery(id+"F0.wireOp",EDGE,"E15.46.0.6"),sQuery(id+"F0.wireOp",EDGE,"E15.46.0.7"),sQuery(id+"F0.wireOp",EDGE,"E15.46.0.8"),sQuery(id+"F0.wireOp",EDGE,"E15.47.0.0"),sQuery(id+"F0.wireOp",EDGE,"E15.47.0.1"),sQuery(id+"F0.wireOp",EDGE,"E15.47.0.2"),sQuery(id+"F0.wireOp",EDGE,"E15.47.0.3"),sQuery(id+"F0.wireOp",EDGE,"E15.47.0.4"),sQuery(id+"F0.wireOp",EDGE,"E15.47.0.5"),sQuery(id+"F0.wireOp",EDGE,"E15.47.0.6"),sQuery(id+"F0.wireOp",EDGE,"E15.47.0.7"),sQuery(id+"F0.wireOp",EDGE,"E15.47.0.8"),sQuery(id+"F0.wireOp",EDGE,"E15.48.0.0"),sQuery(id+"F0.wireOp",EDGE,"E15.48.0.1"),sQuery(id+"F0.wireOp",EDGE,"E15.48.0.2"),sQuery(id+"F0.wireOp",EDGE,"E15.48.0.3"),sQuery(id+"F0.wireOp",EDGE,"E15.48.0.4"),sQuery(id+"F0.wireOp",EDGE,"E15.48.0.5"),sQuery(id+"F0.wireOp",EDGE,"E15.48.0.6"),sQuery(id+"F0.wireOp",EDGE,"E15.48.0.7"),sQuery(id+"F0.wireOp",EDGE,"E15.48.0.8"),sQuery(id+"F0.wireOp",EDGE,"E15.49.0.0"),sQuery(id+"F0.wireOp",EDGE,"E15.49.0.1"),sQuery(id+"F0.wireOp",EDGE,"E15.49.0.2"),sQuery(id+"F0.wireOp",EDGE,"E15.49.0.3"),sQuery(id+"F0.wireOp",EDGE,"E15.49.0.4"),sQuery(id+"F0.wireOp",EDGE,"E15.49.0.5"),sQuery(id+"F0.wireOp",EDGE,"E15.49.0.6"),sQuery(id+"F0.wireOp",EDGE,"E15.49.0.7"),sQuery(id+"F0.wireOp",EDGE,"E15.49.0.8"),sQuery(id+"F0.wireOp",EDGE,"E16")])]});
            hole(context, id + "F7", {"style" : HoleStyle.C_BORE, "endStyle" : HoleEndStyle.THROUGH, "holeDiameter" : 4.83 * mm, "cBoreDiameter" : 9.47 * mm, "cBoreDepth" : 3.38 * mm, "tappedDepth" : 12.7 * mm, "tapClearance" : 3, "locations" : qUnion([Q0, Q1, Q2, Q3, Q4, Q5, Q6, Q7]), "scope" : qUnion([Q8])});
        }
    });
